# Revit family: 879-005X99-001-DN65-600
name_source: partatom
category: Pipe Accessories
units: mm (PartAtom-declared; Revit-internal decimal feet)

## family parameters
Always vertical = Yes
Cut with Voids When Loaded = No
Part Type = Valve - Breaks Into
Round Connector Dimension = Use Diameter
Shared = No
Work Plane-Based = No

## types (42) — shared parameters
879-0065-00-14400559999 = DN65_PN10/16
879-0065-00-144005599A0 = DN65_PN10/16
879-0080-00-14400559999 = DN80_PN10/16
879-0080-00-144005599A0 = DN80_PN10/16
879-0100-00-14400559999 = DN100_PN10/16
879-0100-00-144005599A0 = DN100_PN10/16
879-0125-00-14400559999 = DN125_PN10/16
879-0125-00-144005599A0 = DN125_PN10/16
879-0150-00-14400559999 = DN150_PN10/16
879-0150-00-144005599A0 = DN150_PN10/16
879-0200-00-04400559999 = DN200_PN10
879-0200-00-044005599A0 = DN200_PN10
879-0200-00-14400559999 = DN200_PN16
879-0200-00-144005599A0 = DN200_PN16
879-0250-00-04400559999 = DN250_PN10
879-0250-00-044005599A0 = DN250_PN10
879-0250-00-14400559999 = DN250_PN16
879-0250-00-144005599A0 = DN250_PN16
879-0300-00-04400559999 = DN300_PN10
879-0300-00-044005599A0 = DN300_PN10
879-0300-00-14400559999 = DN300_PN16
879-0300-00-144005599A0 = DN300_PN16
879-0350-00-04400559999 = DN350_PN10
879-0350-00-044005599A0 = DN350_PN10
879-0350-00-14400559999 = DN350_PN16
879-0350-00-144005599A0 = DN350_PN16
879-0400-00-04400559999 = DN400_PN10
879-0400-00-044005599A0 = DN400_PN10
879-0400-00-14400559999 = DN400_PN16
879-0400-00-144005599A0 = DN400_PN16
879-0450-00-04400559999 = DN450_PN10
879-0450-00-044005599A0 = DN450_PN10
879-0450-00-14400559999 = DN450_PN16
879-0450-00-144005599A0 = DN450_PN16
879-0500-00-04400559999 = DN500_PN10
879-0500-00-044005599A0 = DN500_PN10
879-0500-00-14400559999 = DN500_PN16
879-0500-00-144005599A0 = DN500_PN16
879-0600-00-04400559999 = DN600_PN10
879-0600-00-044005599A0 = DN600_PN10
879-0600-00-14400559999 = DN600_PN16
879-0600-00-144005599A0 = DN600_PN16
Body_wall_thickness = 10 mm  [stored 0.0328084 ft]
Description_ = AVK MODULATING FLOAT LEVEL CONTROL VALVE
Search_Table = 879-005X99-001-DN65-600
URL product pages = https://www.avkvalves.com

## per-type parameters (varying)
- 879-0065-00-14400559999_DN65_PN10/16: Body_Collar_Dia=22 mm  [stored 0.0721785 ft]; Body_Collar_Dia_2=15 mm  [stored 0.0492126 ft]; Body_Flange_Dia=83 mm; Body_Flange_Dia_2=88 mm; Body_Height_1=83 mm; Body_Height_2=36 mm  [stored 0.11811 ft]; Body_Height_3=58 mm; Body_Height_4=51 mm; Body_Top_Dia=10 mm  [stored 0.0328084 ft]; Body_Top_Dia_2=8 mm  [stored 0.0262467 ft]; Body_With_Dia=58 mm; Body_With_Dia_1=73 mm; Body_With_Dia_2=73 mm; Bolt_support=223 mm; Bolt_support_2=112 mm; Bolt_support_Dia=12 mm  [stored 0.0393701 ft]; Bolt_support_lenght=53 mm; Bolt_support_lenght_2=63 mm; Bottom_profile=16 mm  [stored 0.0524934 ft]; D1=59 mm; D3=93 mm; DN=65 mm; Fillet_Length=6 mm  [stored 0.019685 ft]; Fillet_Length_2=24 mm  [stored 0.0787402 ft]; Flange_thickness=19 mm  [stored 0.062336 ft]; H3=339 mm; H3_Ref=322 mm; H3_Ref_2=154 mm; ID=33 mm; L=290 mm; PG_Dia=33 mm; PG_Ref=55 mm; PG_depth=8 mm  [stored 0.0262467 ft]; PG_height=211 mm; PG_height_1=194 mm; PG_ref=43 mm  [stored 0.141076 ft]; PR_1=20 mm  [stored 0.0656168 ft]; P_lenght=39 mm  [stored 0.127953 ft]; Pilot_Dia_1=18 mm; Pilot_Dia_2=35 mm  [stored 0.114829 ft]; Pilot_Dia_3=12 mm  [stored 0.0393701 ft]; Pilot_Dia_4=6 mm  [stored 0.019685 ft]; Pilot_Dia_5=4 mm  [stored 0.0131234 ft]; Pilot_top_1=219 mm; Pilot_top_ref=17 mm; Profile1_Height=117 mm; Profile1_Length=25 mm  [stored 0.082021 ft]; Profile1_Length_2=17 mm; Profile_Dia=6 mm  [stored 0.019685 ft]; Profile_Dia_2=6 mm  [stored 0.019685 ft]; Profile_Dia_3=12 mm  [stored 0.0393701 ft]; Profile_height ref=41 mm  [stored 0.134514 ft]; T_Height=89 mm; T_Height_2=76 mm; T_Height_Ref_1=13 mm  [stored 0.0426509 ft]; T_Height_Ref_2=15 mm  [stored 0.0492126 ft]; Top_Profile=134 mm; Top_Profile_Ref=139 mm; W=244 mm; W_Ref=238 mm
- 879-0065-00-144005599A0_DN65_PN10/16: Body_Collar_Dia=22 mm  [stored 0.0721785 ft]; Body_Collar_Dia_2=15 mm  [stored 0.0492126 ft]; Body_Flange_Dia=83 mm; Body_Flange_Dia_2=88 mm; Body_Height_1=83 mm; Body_Height_2=36 mm  [stored 0.11811 ft]; Body_Height_3=100 mm; Body_Height_4=51 mm; Body_Top_Dia=10 mm  [stored 0.0328084 ft]; Body_Top_Dia_2=8 mm  [stored 0.0262467 ft]; Body_With_Dia=58 mm; Body_With_Dia_1=73 mm; Body_With_Dia_2=73 mm; Bolt_support=223 mm; Bolt_support_2=112 mm; Bolt_support_Dia=12 mm  [stored 0.0393701 ft]; Bolt_support_lenght=53 mm; Bolt_support_lenght_2=63 mm; Bottom_profile=16 mm  [stored 0.0524934 ft]; D1=59 mm; D3=93 mm; DN=65 mm; Fillet_Length=6 mm  [stored 0.019685 ft]; Fillet_Length_2=24 mm  [stored 0.0787402 ft]; Flange_thickness=19 mm  [stored 0.062336 ft]; H3=424 mm; H3_Ref=385 mm; H3_Ref_2=154 mm; ID=33 mm; L=290 mm; PG_Dia=33 mm; PG_Ref=55 mm; PG_depth=8 mm  [stored 0.0262467 ft]; PG_height=244 mm; PG_height_1=227 mm; PG_ref=43 mm  [stored 0.141076 ft]; PR_1=35 mm  [stored 0.114829 ft]; P_lenght=39 mm  [stored 0.127953 ft]; Pilot_Dia_1=18 mm; Pilot_Dia_2=35 mm  [stored 0.114829 ft]; Pilot_Dia_3=12 mm  [stored 0.0393701 ft]; Pilot_Dia_4=6 mm  [stored 0.019685 ft]; Pilot_Dia_5=4 mm  [stored 0.0131234 ft]; Pilot_top_1=283 mm; Pilot_top_ref=39 mm  [stored 0.127953 ft]; Profile1_Height=135 mm; Profile1_Length=25 mm  [stored 0.082021 ft]; Profile1_Length_2=17 mm; Profile_Dia=6 mm  [stored 0.019685 ft]; Profile_Dia_2=6 mm  [stored 0.019685 ft]; Profile_Dia_3=12 mm  [stored 0.0393701 ft]; Profile_height ref=41 mm  [stored 0.134514 ft]; T_Height=156 mm; T_Height_2=133 mm; T_Height_Ref_1=22 mm  [stored 0.0721785 ft]; T_Height_Ref_2=26 mm; Top_Profile=134 mm; Top_Profile_Ref=139 mm; W=244 mm; W_Ref=238 mm
- 879-0080-00-14400559999_DN80_PN10/16: Body_Collar_Dia=24 mm  [stored 0.0787402 ft]; Body_Collar_Dia_2=16 mm  [stored 0.0524934 ft]; Body_Flange_Dia=89 mm; Body_Flange_Dia_2=94 mm; Body_Height_1=89 mm; Body_Height_2=39 mm  [stored 0.127953 ft]; Body_Height_3=62 mm; Body_Height_4=54 mm; Body_Top_Dia=10 mm  [stored 0.0328084 ft]; Body_Top_Dia_2=9 mm  [stored 0.0295276 ft]; Body_With_Dia=62 mm; Body_With_Dia_1=78 mm; Body_With_Dia_2=78 mm; Bolt_support=238 mm; Bolt_support_2=119 mm; Bolt_support_Dia=12 mm  [stored 0.0393701 ft]; Bolt_support_lenght=60 mm; Bolt_support_lenght_2=70 mm; Bottom_profile=20 mm  [stored 0.0656168 ft]; D1=66 mm; D3=100 mm; DN=80 mm; Fillet_Length=6 mm  [stored 0.019685 ft]; Fillet_Length_2=24 mm  [stored 0.0787402 ft]; Flange_thickness=19 mm  [stored 0.062336 ft]; H3=362 mm; H3_Ref=343 mm; H3_Ref_2=162 mm; ID=40 mm  [stored 0.131234 ft]; L=310 mm; PG_Dia=40 mm  [stored 0.131234 ft]; PG_Ref=59 mm; PG_depth=8 mm  [stored 0.0262467 ft]; PG_height=242 mm; PG_height_1=222 mm; PG_ref=50 mm; PR_1=17 mm; P_lenght=43 mm  [stored 0.141076 ft]; Pilot_Dia_1=20 mm  [stored 0.0656168 ft]; Pilot_Dia_2=39 mm  [stored 0.127953 ft]; Pilot_Dia_3=13 mm  [stored 0.0426509 ft]; Pilot_Dia_4=7 mm  [stored 0.0229659 ft]; Pilot_Dia_5=4 mm  [stored 0.0131234 ft]; Pilot_top_1=233 mm; Pilot_top_ref=19 mm  [stored 0.062336 ft]; Profile1_Height=144 mm; Profile1_Length=27 mm; Profile1_Length_2=18 mm; Profile_Dia=6 mm  [stored 0.019685 ft]; Profile_Dia_2=6 mm  [stored 0.019685 ft]; Profile_Dia_3=12 mm  [stored 0.0393701 ft]; Profile_height ref=41 mm  [stored 0.134514 ft]; T_Height=77 mm; T_Height_2=66 mm; T_Height_Ref_1=11 mm  [stored 0.0360892 ft]; T_Height_Ref_2=13 mm  [stored 0.0426509 ft]; Top_Profile=143 mm; Top_Profile_Ref=148 mm; W=257 mm; W_Ref=251 mm
- 879-0080-00-144005599A0_DN80_PN10/16: Body_Collar_Dia=24 mm  [stored 0.0787402 ft]; Body_Collar_Dia_2=16 mm  [stored 0.0524934 ft]; Body_Flange_Dia=89 mm; Body_Flange_Dia_2=94 mm; Body_Height_1=89 mm; Body_Height_2=39 mm  [stored 0.127953 ft]; Body_Height_3=110 mm; Body_Height_4=54 mm; Body_Top_Dia=10 mm  [stored 0.0328084 ft]; Body_Top_Dia_2=9 mm  [stored 0.0295276 ft]; Body_With_Dia=62 mm; Body_With_Dia_1=78 mm; Body_With_Dia_2=78 mm; Bolt_support=238 mm; Bolt_support_2=119 mm; Bolt_support_Dia=12 mm  [stored 0.0393701 ft]; Bolt_support_lenght=60 mm; Bolt_support_lenght_2=70 mm; Bottom_profile=20 mm  [stored 0.0656168 ft]; D1=66 mm; D3=100 mm; DN=80 mm; Fillet_Length=6 mm  [stored 0.019685 ft]; Fillet_Length_2=24 mm  [stored 0.0787402 ft]; Flange_thickness=19 mm  [stored 0.062336 ft]; H3=447 mm; H3_Ref=410 mm; H3_Ref_2=162 mm; ID=40 mm  [stored 0.131234 ft]; L=310 mm; PG_Dia=40 mm  [stored 0.131234 ft]; PG_Ref=59 mm; PG_depth=8 mm  [stored 0.0262467 ft]; PG_height=253 mm; PG_height_1=233 mm; PG_ref=50 mm; PR_1=39 mm  [stored 0.127953 ft]; P_lenght=43 mm  [stored 0.141076 ft]; Pilot_Dia_1=20 mm  [stored 0.0656168 ft]; Pilot_Dia_2=39 mm  [stored 0.127953 ft]; Pilot_Dia_3=13 mm  [stored 0.0426509 ft]; Pilot_Dia_4=7 mm  [stored 0.0229659 ft]; Pilot_Dia_5=4 mm  [stored 0.0131234 ft]; Pilot_top_1=300 mm; Pilot_top_ref=37 mm; Profile1_Height=133 mm; Profile1_Length=27 mm; Profile1_Length_2=18 mm; Profile_Dia=6 mm  [stored 0.019685 ft]; Profile_Dia_2=6 mm  [stored 0.019685 ft]; Profile_Dia_3=12 mm  [stored 0.0393701 ft]; Profile_height ref=41 mm  [stored 0.134514 ft]; T_Height=173 mm; T_Height_2=148 mm; T_Height_Ref_1=25 mm  [stored 0.082021 ft]; T_Height_Ref_2=29 mm; Top_Profile=143 mm; Top_Profile_Ref=148 mm; W=257 mm; W_Ref=251 mm
- 879-0100-00-14400559999_DN100_PN10/16: Body_Collar_Dia=27 mm; Body_Collar_Dia_2=18 mm; Body_Flange_Dia=100 mm; Body_Flange_Dia_2=106 mm; Body_Height_1=100 mm; Body_Height_2=44 mm; Body_Height_3=50 mm; Body_Height_4=59 mm; Body_Top_Dia=12 mm  [stored 0.0393701 ft]; Body_Top_Dia_2=10 mm  [stored 0.0328084 ft]; Body_With_Dia=70 mm; Body_With_Dia_1=88 mm; Body_With_Dia_2=88 mm; Bolt_support=269 mm; Bolt_support_2=135 mm; Bolt_support_Dia=12 mm  [stored 0.0393701 ft]; Bolt_support_lenght=70 mm; Bolt_support_lenght_2=80 mm; Bottom_profile=25 mm  [stored 0.082021 ft]; D1=78 mm; D3=110 mm; DN=100 mm; Fillet_Length=6 mm  [stored 0.019685 ft]; Fillet_Length_2=24 mm  [stored 0.0787402 ft]; Flange_thickness=19 mm  [stored 0.062336 ft]; H3=376 mm; H3_Ref=357 mm; H3_Ref_2=179 mm; ID=50 mm; L=350 mm; PG_Dia=50 mm; PG_Ref=67 mm; PG_depth=8 mm  [stored 0.0262467 ft]; PG_height=258 mm; PG_height_1=233 mm; PG_ref=60 mm; PR_1=17 mm; P_lenght=48 mm; Pilot_Dia_1=22 mm  [stored 0.0721785 ft]; Pilot_Dia_2=44 mm; Pilot_Dia_3=15 mm  [stored 0.0492126 ft]; Pilot_Dia_4=7 mm  [stored 0.0229659 ft]; Pilot_Dia_5=5 mm  [stored 0.0164042 ft]; Pilot_top_1=237 mm; Pilot_top_ref=19 mm  [stored 0.062336 ft]; Profile1_Height=150 mm; Profile1_Length=30 mm  [stored 0.0984252 ft]; Profile1_Length_2=20 mm  [stored 0.0656168 ft]; Profile_Dia=6 mm  [stored 0.019685 ft]; Profile_Dia_2=6 mm  [stored 0.019685 ft]; Profile_Dia_3=12 mm  [stored 0.0393701 ft]; Profile_height ref=41 mm  [stored 0.134514 ft]; T_Height=75 mm; T_Height_2=64 mm; T_Height_Ref_1=11 mm  [stored 0.0360892 ft]; T_Height_Ref_2=13 mm  [stored 0.0426509 ft]; Top_Profile=162 mm; Top_Profile_Ref=167 mm; W=276 mm; W_Ref=270 mm
- 879-0100-00-144005599A0_DN100_PN10/16: Body_Collar_Dia=27 mm; Body_Collar_Dia_2=18 mm; Body_Flange_Dia=100 mm; Body_Flange_Dia_2=106 mm; Body_Height_1=100 mm; Body_Height_2=44 mm; Body_Height_3=100 mm; Body_Height_4=59 mm; Body_Top_Dia=12 mm  [stored 0.0393701 ft]; Body_Top_Dia_2=10 mm  [stored 0.0328084 ft]; Body_With_Dia=70 mm; Body_With_Dia_1=88 mm; Body_With_Dia_2=88 mm; Bolt_support=269 mm; Bolt_support_2=135 mm; Bolt_support_Dia=12 mm  [stored 0.0393701 ft]; Bolt_support_lenght=70 mm; Bolt_support_lenght_2=80 mm; Bottom_profile=25 mm  [stored 0.082021 ft]; D1=78 mm; D3=110 mm; DN=100 mm; Fillet_Length=6 mm  [stored 0.019685 ft]; Fillet_Length_2=24 mm  [stored 0.0787402 ft]; Flange_thickness=19 mm  [stored 0.062336 ft]; H3=461 mm; H3_Ref=425 mm; H3_Ref_2=179 mm; ID=50 mm; L=350 mm; PG_Dia=50 mm; PG_Ref=67 mm; PG_depth=8 mm  [stored 0.0262467 ft]; PG_height=270 mm; PG_height_1=245 mm; PG_ref=60 mm; PR_1=38 mm; P_lenght=48 mm; Pilot_Dia_1=22 mm  [stored 0.0721785 ft]; Pilot_Dia_2=44 mm; Pilot_Dia_3=15 mm  [stored 0.0492126 ft]; Pilot_Dia_4=7 mm  [stored 0.0229659 ft]; Pilot_Dia_5=5 mm  [stored 0.0164042 ft]; Pilot_top_1=305 mm; Pilot_top_ref=36 mm  [stored 0.11811 ft]; Profile1_Height=141 mm; Profile1_Length=30 mm  [stored 0.0984252 ft]; Profile1_Length_2=20 mm  [stored 0.0656168 ft]; Profile_Dia=6 mm  [stored 0.019685 ft]; Profile_Dia_2=6 mm  [stored 0.019685 ft]; Profile_Dia_3=12 mm  [stored 0.0393701 ft]; Profile_height ref=41 mm  [stored 0.134514 ft]; T_Height=169 mm; T_Height_2=145 mm; T_Height_Ref_1=24 mm  [stored 0.0787402 ft]; T_Height_Ref_2=28 mm  [stored 0.0918635 ft]; Top_Profile=162 mm; Top_Profile_Ref=167 mm; W=276 mm; W_Ref=270 mm
- 879-0125-00-14400559999_DN125_PN10/16: Body_Collar_Dia=31 mm  [stored 0.101706 ft]; Body_Collar_Dia_2=20 mm  [stored 0.0656168 ft]; Body_Flange_Dia=114 mm; Body_Flange_Dia_2=121 mm; Body_Height_1=114 mm; Body_Height_2=50 mm; Body_Height_3=35 mm  [stored 0.114829 ft]; Body_Height_4=65 mm; Body_Top_Dia=13 mm  [stored 0.0426509 ft]; Body_Top_Dia_2=11 mm  [stored 0.0360892 ft]; Body_With_Dia=80 mm; Body_With_Dia_1=100 mm; Body_With_Dia_2=100 mm; Bolt_support=308 mm; Bolt_support_2=154 mm; Bolt_support_Dia=12 mm  [stored 0.0393701 ft]; Bolt_support_lenght=83 mm; Bolt_support_lenght_2=93 mm; Bottom_profile=31 mm  [stored 0.101706 ft]; D1=92 mm; D3=125 mm; DN=125 mm; Fillet_Length=6 mm  [stored 0.019685 ft]; Fillet_Length_2=24 mm  [stored 0.0787402 ft]; Flange_thickness=19 mm  [stored 0.062336 ft]; H3=395 mm; H3_Ref=377 mm; H3_Ref_2=199 mm; ID=63 mm; L=400 mm; PG_Dia=63 mm; PG_Ref=76 mm; PG_depth=8 mm  [stored 0.0262467 ft]; PG_height=283 mm; PG_height_1=252 mm; PG_ref=73 mm; PR_1=14 mm  [stored 0.0459318 ft]; P_lenght=56 mm; Pilot_Dia_1=26 mm; Pilot_Dia_2=51 mm; Pilot_Dia_3=17 mm; Pilot_Dia_4=9 mm  [stored 0.0295276 ft]; Pilot_Dia_5=6 mm  [stored 0.019685 ft]; Pilot_top_1=242 mm; Pilot_top_ref=18 mm; Profile1_Height=165 mm; Profile1_Length=34 mm; Profile1_Length_2=23 mm  [stored 0.0754593 ft]; Profile_Dia=6 mm  [stored 0.019685 ft]; Profile_Dia_2=6 mm  [stored 0.019685 ft]; Profile_Dia_3=12 mm  [stored 0.0393701 ft]; Profile_height ref=41 mm  [stored 0.134514 ft]; T_Height=64 mm; T_Height_2=55 mm; T_Height_Ref_1=9 mm  [stored 0.0295276 ft]; T_Height_Ref_2=11 mm  [stored 0.0360892 ft]; Top_Profile=185 mm; Top_Profile_Ref=190 mm; W=296 mm; W_Ref=290 mm
- 879-0125-00-144005599A0_DN125_PN10/16: Body_Collar_Dia=31 mm  [stored 0.101706 ft]; Body_Collar_Dia_2=20 mm  [stored 0.0656168 ft]; Body_Flange_Dia=114 mm; Body_Flange_Dia_2=121 mm; Body_Height_1=114 mm; Body_Height_2=50 mm; Body_Height_3=90 mm; Body_Height_4=65 mm; Body_Top_Dia=13 mm  [stored 0.0426509 ft]; Body_Top_Dia_2=11 mm  [stored 0.0360892 ft]; Body_With_Dia=80 mm; Body_With_Dia_1=100 mm; Body_With_Dia_2=100 mm; Bolt_support=308 mm; Bolt_support_2=154 mm; Bolt_support_Dia=12 mm  [stored 0.0393701 ft]; Bolt_support_lenght=83 mm; Bolt_support_lenght_2=93 mm; Bottom_profile=31 mm  [stored 0.101706 ft]; D1=92 mm; D3=125 mm; DN=125 mm; Fillet_Length=6 mm  [stored 0.019685 ft]; Fillet_Length_2=24 mm  [stored 0.0787402 ft]; Flange_thickness=19 mm  [stored 0.062336 ft]; H3=480 mm; H3_Ref=447 mm; H3_Ref_2=199 mm; ID=63 mm; L=400 mm; PG_Dia=63 mm; PG_Ref=76 mm; PG_depth=8 mm  [stored 0.0262467 ft]; PG_height=302 mm; PG_height_1=271 mm; PG_ref=73 mm; PR_1=34 mm; P_lenght=56 mm; Pilot_Dia_1=26 mm; Pilot_Dia_2=51 mm; Pilot_Dia_3=17 mm; Pilot_Dia_4=9 mm  [stored 0.0295276 ft]; Pilot_Dia_5=6 mm  [stored 0.019685 ft]; Pilot_top_1=312 mm; Pilot_top_ref=33 mm; Profile1_Height=165 mm; Profile1_Length=34 mm; Profile1_Length_2=23 mm  [stored 0.0754593 ft]; Profile_Dia=6 mm  [stored 0.019685 ft]; Profile_Dia_2=6 mm  [stored 0.019685 ft]; Profile_Dia_3=12 mm  [stored 0.0393701 ft]; Profile_height ref=41 mm  [stored 0.134514 ft]; T_Height=149 mm; T_Height_2=128 mm; T_Height_Ref_1=21 mm  [stored 0.0688976 ft]; T_Height_Ref_2=25 mm  [stored 0.082021 ft]; Top_Profile=185 mm; Top_Profile_Ref=190 mm; W=296 mm; W_Ref=290 mm
- 879-0150-00-14400559999_DN150_PN10/16: Body_Collar_Dia=37 mm; Body_Collar_Dia_2=24 mm  [stored 0.0787402 ft]; Body_Flange_Dia=137 mm; Body_Flange_Dia_2=145 mm; Body_Height_1=137 mm; Body_Height_2=60 mm; Body_Height_3=30 mm  [stored 0.0984252 ft]; Body_Height_4=75 mm; Body_Top_Dia=16 mm  [stored 0.0524934 ft]; Body_Top_Dia_2=13 mm  [stored 0.0426509 ft]; Body_With_Dia=96 mm; Body_With_Dia_1=120 mm; Body_With_Dia_2=120 mm; Bolt_support=369 mm; Bolt_support_2=185 mm; Bolt_support_Dia=16 mm  [stored 0.0524934 ft]; Bolt_support_lenght=95 mm; Bolt_support_lenght_2=105 mm; Bottom_profile=38 mm; D1=106 mm; D3=143 mm; DN=150 mm; Fillet_Length=8 mm  [stored 0.0262467 ft]; Fillet_Length_2=32 mm  [stored 0.104987 ft]; Flange_thickness=19 mm  [stored 0.062336 ft]; H3=429 mm; H3_Ref=417 mm; H3_Ref_2=232 mm; ID=75 mm; L=480 mm; PG_Dia=50 mm; PG_Ref=91 mm; PG_depth=11 mm  [stored 0.0360892 ft]; PG_height=299 mm; PG_height_1=274 mm; PG_ref=85 mm; PR_1=11 mm  [stored 0.0360892 ft]; P_lenght=68 mm; Pilot_Dia_1=31 mm  [stored 0.101706 ft]; Pilot_Dia_2=62 mm; Pilot_Dia_3=21 mm  [stored 0.0688976 ft]; Pilot_Dia_4=10 mm  [stored 0.0328084 ft]; Pilot_Dia_5=7 mm  [stored 0.0229659 ft]; Pilot_top_1=264 mm; Pilot_top_ref=12 mm  [stored 0.0393701 ft]; Profile1_Height=195 mm; Profile1_Length=39 mm  [stored 0.127953 ft]; Profile1_Length_2=26 mm; Profile_Dia=8 mm  [stored 0.0262467 ft]; Profile_Dia_2=8 mm  [stored 0.0262467 ft]; Profile_Dia_3=16 mm  [stored 0.0524934 ft]; Profile_height ref=43 mm  [stored 0.141076 ft]; T_Height=49 mm; T_Height_2=42 mm  [stored 0.137795 ft]; T_Height_Ref_1=7 mm  [stored 0.0229659 ft]; T_Height_Ref_2=8 mm  [stored 0.0262467 ft]; Top_Profile=222 mm; Top_Profile_Ref=227 mm; W=302 mm; W_Ref=294 mm
- 879-0150-00-144005599A0_DN150_PN10/16: Body_Collar_Dia=37 mm; Body_Collar_Dia_2=24 mm  [stored 0.0787402 ft]; Body_Flange_Dia=137 mm; Body_Flange_Dia_2=145 mm; Body_Height_1=137 mm; Body_Height_2=60 mm; Body_Height_3=115 mm; Body_Height_4=75 mm; Body_Top_Dia=16 mm  [stored 0.0524934 ft]; Body_Top_Dia_2=13 mm  [stored 0.0426509 ft]; Body_With_Dia=96 mm; Body_With_Dia_1=120 mm; Body_With_Dia_2=120 mm; Bolt_support=369 mm; Bolt_support_2=185 mm; Bolt_support_Dia=16 mm  [stored 0.0524934 ft]; Bolt_support_lenght=95 mm; Bolt_support_lenght_2=105 mm; Bottom_profile=38 mm; D1=106 mm; D3=143 mm; DN=150 mm; Fillet_Length=8 mm  [stored 0.0262467 ft]; Fillet_Length_2=32 mm  [stored 0.104987 ft]; Flange_thickness=19 mm  [stored 0.062336 ft]; H3=514 mm; H3_Ref=502 mm; H3_Ref_2=232 mm; ID=75 mm; L=480 mm; PG_Dia=50 mm; PG_Ref=91 mm; PG_depth=11 mm  [stored 0.0360892 ft]; PG_height=318 mm; PG_height_1=293 mm; PG_ref=85 mm; PR_1=30 mm  [stored 0.0984252 ft]; P_lenght=68 mm; Pilot_Dia_1=31 mm  [stored 0.101706 ft]; Pilot_Dia_2=62 mm; Pilot_Dia_3=21 mm  [stored 0.0688976 ft]; Pilot_Dia_4=10 mm  [stored 0.0328084 ft]; Pilot_Dia_5=7 mm  [stored 0.0229659 ft]; Pilot_top_1=349 mm; Pilot_top_ref=12 mm  [stored 0.0393701 ft]; Profile1_Height=195 mm; Profile1_Length=39 mm  [stored 0.127953 ft]; Profile1_Length_2=26 mm; Profile_Dia=8 mm  [stored 0.0262467 ft]; Profile_Dia_2=8 mm  [stored 0.0262467 ft]; Profile_Dia_3=16 mm  [stored 0.0524934 ft]; Profile_height ref=43 mm  [stored 0.141076 ft]; T_Height=134 mm; T_Height_2=114 mm; T_Height_Ref_1=19 mm  [stored 0.062336 ft]; T_Height_Ref_2=22 mm  [stored 0.0721785 ft]; Top_Profile=222 mm; Top_Profile_Ref=227 mm; W=302 mm; W_Ref=294 mm
- 879-0200-00-04400559999_DN200_PN10: Body_Collar_Dia=46 mm; Body_Collar_Dia_2=30 mm  [stored 0.0984252 ft]; Body_Flange_Dia=171 mm; Body_Flange_Dia_2=182 mm; Body_Height_1=171 mm; Body_Height_2=75 mm; Body_Height_3=100 mm; Body_Height_4=90 mm; Body_Top_Dia=20 mm  [stored 0.0656168 ft]; Body_Top_Dia_2=17 mm; Body_With_Dia=120 mm; Body_With_Dia_1=150 mm; Body_With_Dia_2=150 mm; Bolt_support=462 mm; Bolt_support_2=231 mm; Bolt_support_Dia=20 mm  [stored 0.0656168 ft]; Bolt_support_lenght=120 mm; Bolt_support_lenght_2=130 mm; Bottom_profile=50 mm; D1=133 mm; D3=170 mm; DN=200 mm; Fillet_Length=10 mm  [stored 0.0328084 ft]; Fillet_Length_2=40 mm  [stored 0.131234 ft]; Flange_thickness=20 mm  [stored 0.0656168 ft]; H3=588 mm; H3_Ref=570 mm; H3_Ref_2=281 mm; ID=100 mm; L=600 mm; PG_Dia=67 mm; PG_Ref=114 mm; PG_depth=14 mm  [stored 0.0459318 ft]; PG_height=380 mm; PG_height_1=347 mm; PG_ref=110 mm; PR_1=31 mm  [stored 0.101706 ft]; P_lenght=85 mm; Pilot_Dia_1=39 mm  [stored 0.127953 ft]; Pilot_Dia_2=77 mm; Pilot_Dia_3=26 mm; Pilot_Dia_4=13 mm  [stored 0.0426509 ft]; Pilot_Dia_5=9 mm  [stored 0.0295276 ft]; Pilot_top_1=390 mm; Pilot_top_ref=18 mm; Profile1_Height=238 mm; Profile1_Length=46 mm; Profile1_Length_2=31 mm  [stored 0.101706 ft]; Profile_Dia=10 mm  [stored 0.0328084 ft]; Profile_Dia_2=10 mm  [stored 0.0328084 ft]; Profile_Dia_3=20 mm  [stored 0.0656168 ft]; Profile_height ref=45 mm; T_Height=135 mm; T_Height_2=116 mm; T_Height_Ref_1=19 mm  [stored 0.062336 ft]; T_Height_Ref_2=23 mm  [stored 0.0754593 ft]; Top_Profile=277 mm; Top_Profile_Ref=282 mm; W=410 mm; W_Ref=400 mm
- 879-0200-00-044005599A0_DN200_PN10: Body_Collar_Dia=46 mm; Body_Collar_Dia_2=30 mm  [stored 0.0984252 ft]; Body_Flange_Dia=171 mm; Body_Flange_Dia_2=182 mm; Body_Height_1=171 mm; Body_Height_2=75 mm; Body_Height_3=170 mm; Body_Height_4=90 mm; Body_Top_Dia=20 mm  [stored 0.0656168 ft]; Body_Top_Dia_2=17 mm; Body_With_Dia=120 mm; Body_With_Dia_1=150 mm; Body_With_Dia_2=150 mm; Bolt_support=462 mm; Bolt_support_2=231 mm; Bolt_support_Dia=20 mm  [stored 0.0656168 ft]; Bolt_support_lenght=120 mm; Bolt_support_lenght_2=130 mm; Bottom_profile=50 mm; D1=133 mm; D3=170 mm; DN=200 mm; Fillet_Length=10 mm  [stored 0.0328084 ft]; Fillet_Length_2=40 mm  [stored 0.131234 ft]; Flange_thickness=20 mm  [stored 0.0656168 ft]; H3=688 mm; H3_Ref=655 mm; H3_Ref_2=281 mm; ID=100 mm; L=600 mm; PG_Dia=67 mm; PG_Ref=114 mm; PG_depth=14 mm  [stored 0.0459318 ft]; PG_height=404 mm; PG_height_1=371 mm; PG_ref=110 mm; PR_1=53 mm; P_lenght=85 mm; Pilot_Dia_1=39 mm  [stored 0.127953 ft]; Pilot_Dia_2=77 mm; Pilot_Dia_3=26 mm; Pilot_Dia_4=13 mm  [stored 0.0426509 ft]; Pilot_Dia_5=9 mm  [stored 0.0295276 ft]; Pilot_top_1=475 mm; Pilot_top_ref=33 mm; Profile1_Height=240 mm; Profile1_Length=46 mm; Profile1_Length_2=31 mm  [stored 0.101706 ft]; Profile_Dia=10 mm  [stored 0.0328084 ft]; Profile_Dia_2=10 mm  [stored 0.0328084 ft]; Profile_Dia_3=20 mm  [stored 0.0656168 ft]; Profile_height ref=45 mm; T_Height=233 mm; T_Height_2=200 mm; T_Height_Ref_1=33 mm; T_Height_Ref_2=39 mm  [stored 0.127953 ft]; Top_Profile=277 mm; Top_Profile_Ref=282 mm; W=410 mm; W_Ref=400 mm
- 879-0200-00-14400559999_DN200_PN16: Body_Collar_Dia=46 mm; Body_Collar_Dia_2=30 mm  [stored 0.0984252 ft]; Body_Flange_Dia=171 mm; Body_Flange_Dia_2=182 mm; Body_Height_1=171 mm; Body_Height_2=75 mm; Body_Height_3=100 mm; Body_Height_4=90 mm; Body_Top_Dia=20 mm  [stored 0.0656168 ft]; Body_Top_Dia_2=17 mm; Body_With_Dia=120 mm; Body_With_Dia_1=150 mm; Body_With_Dia_2=150 mm; Bolt_support=462 mm; Bolt_support_2=231 mm; Bolt_support_Dia=20 mm  [stored 0.0656168 ft]; Bolt_support_lenght=120 mm; Bolt_support_lenght_2=130 mm; Bottom_profile=50 mm; D1=133 mm; D3=170 mm; DN=200 mm; Fillet_Length=10 mm  [stored 0.0328084 ft]; Fillet_Length_2=40 mm  [stored 0.131234 ft]; Flange_thickness=20 mm  [stored 0.0656168 ft]; H3=588 mm; H3_Ref=570 mm; H3_Ref_2=281 mm; ID=100 mm; L=600 mm; PG_Dia=67 mm; PG_Ref=114 mm; PG_depth=14 mm  [stored 0.0459318 ft]; PG_height=380 mm; PG_height_1=347 mm; PG_ref=110 mm; PR_1=31 mm  [stored 0.101706 ft]; P_lenght=85 mm; Pilot_Dia_1=39 mm  [stored 0.127953 ft]; Pilot_Dia_2=77 mm; Pilot_Dia_3=26 mm; Pilot_Dia_4=13 mm  [stored 0.0426509 ft]; Pilot_Dia_5=9 mm  [stored 0.0295276 ft]; Pilot_top_1=390 mm; Pilot_top_ref=18 mm; Profile1_Height=238 mm; Profile1_Length=46 mm; Profile1_Length_2=31 mm  [stored 0.101706 ft]; Profile_Dia=10 mm  [stored 0.0328084 ft]; Profile_Dia_2=10 mm  [stored 0.0328084 ft]; Profile_Dia_3=20 mm  [stored 0.0656168 ft]; Profile_height ref=45 mm; T_Height=135 mm; T_Height_2=116 mm; T_Height_Ref_1=19 mm  [stored 0.062336 ft]; T_Height_Ref_2=23 mm  [stored 0.0754593 ft]; Top_Profile=277 mm; Top_Profile_Ref=282 mm; W=410 mm; W_Ref=400 mm
- 879-0200-00-144005599A0_DN200_PN16: Body_Collar_Dia=46 mm; Body_Collar_Dia_2=30 mm  [stored 0.0984252 ft]; Body_Flange_Dia=171 mm; Body_Flange_Dia_2=182 mm; Body_Height_1=171 mm; Body_Height_2=75 mm; Body_Height_3=165 mm; Body_Height_4=90 mm; Body_Top_Dia=20 mm  [stored 0.0656168 ft]; Body_Top_Dia_2=17 mm; Body_With_Dia=120 mm; Body_With_Dia_1=150 mm; Body_With_Dia_2=150 mm; Bolt_support=462 mm; Bolt_support_2=231 mm; Bolt_support_Dia=20 mm  [stored 0.0656168 ft]; Bolt_support_lenght=120 mm; Bolt_support_lenght_2=130 mm; Bottom_profile=50 mm; D1=133 mm; D3=170 mm; DN=200 mm; Fillet_Length=10 mm  [stored 0.0328084 ft]; Fillet_Length_2=40 mm  [stored 0.131234 ft]; Flange_thickness=20 mm  [stored 0.0656168 ft]; H3=688 mm; H3_Ref=652 mm; H3_Ref_2=281 mm; ID=100 mm; L=600 mm; PG_Dia=67 mm; PG_Ref=114 mm; PG_depth=14 mm  [stored 0.0459318 ft]; PG_height=404 mm; PG_height_1=371 mm; PG_ref=110 mm; PR_1=53 mm; P_lenght=85 mm; Pilot_Dia_1=39 mm  [stored 0.127953 ft]; Pilot_Dia_2=77 mm; Pilot_Dia_3=26 mm; Pilot_Dia_4=13 mm  [stored 0.0426509 ft]; Pilot_Dia_5=9 mm  [stored 0.0295276 ft]; Pilot_top_1=472 mm; Pilot_top_ref=36 mm  [stored 0.11811 ft]; Profile1_Height=240 mm; Profile1_Length=46 mm; Profile1_Length_2=31 mm  [stored 0.101706 ft]; Profile_Dia=10 mm  [stored 0.0328084 ft]; Profile_Dia_2=10 mm  [stored 0.0328084 ft]; Profile_Dia_3=20 mm  [stored 0.0656168 ft]; Profile_height ref=45 mm; T_Height=233 mm; T_Height_2=200 mm; T_Height_Ref_1=33 mm; T_Height_Ref_2=39 mm  [stored 0.127953 ft]; Top_Profile=277 mm; Top_Profile_Ref=282 mm; W=410 mm; W_Ref=400 mm
- 879-0250-00-04400559999_DN250_PN10: Body_Collar_Dia=56 mm; Body_Collar_Dia_2=37 mm; Body_Flange_Dia=209 mm; Body_Flange_Dia_2=221 mm; Body_Height_1=209 mm; Body_Height_2=91 mm; Body_Height_3=81 mm; Body_Height_4=106 mm; Body_Top_Dia=24 mm  [stored 0.0787402 ft]; Body_Top_Dia_2=20 mm  [stored 0.0656168 ft]; Body_With_Dia=146 mm; Body_With_Dia_1=183 mm; Body_With_Dia_2=183 mm; Bolt_support=562 mm; Bolt_support_2=281 mm; Bolt_support_Dia=20 mm  [stored 0.0656168 ft]; Bolt_support_lenght=145 mm; Bolt_support_lenght_2=155 mm; Bottom_profile=63 mm; D1=160 mm; D3=198 mm; DN=250 mm; Fillet_Length=10 mm  [stored 0.0328084 ft]; Fillet_Length_2=40 mm  [stored 0.131234 ft]; Flange_thickness=22 mm  [stored 0.0721785 ft]; H3=706 mm; H3_Ref=660 mm; H3_Ref_2=335 mm; ID=125 mm; L=730 mm; PG_Dia=83 mm; PG_Ref=139 mm; PG_depth=14 mm  [stored 0.0459318 ft]; PG_height=446 mm; PG_height_1=404 mm; PG_ref=135 mm; PR_1=43 mm  [stored 0.141076 ft]; P_lenght=101 mm; Pilot_Dia_1=46 mm; Pilot_Dia_2=92 mm; Pilot_Dia_3=31 mm  [stored 0.101706 ft]; Pilot_Dia_4=15 mm  [stored 0.0492126 ft]; Pilot_Dia_5=10 mm  [stored 0.0328084 ft]; Pilot_top_1=452 mm; Pilot_top_ref=46 mm; Profile1_Height=275 mm; Profile1_Length=53 mm; Profile1_Length_2=36 mm  [stored 0.11811 ft]; Profile_Dia=10 mm  [stored 0.0328084 ft]; Profile_Dia_2=10 mm  [stored 0.0328084 ft]; Profile_Dia_3=20 mm  [stored 0.0656168 ft]; Profile_height ref=45 mm; T_Height=189 mm; T_Height_2=162 mm; T_Height_Ref_1=27 mm; T_Height_Ref_2=31 mm  [stored 0.101706 ft]; Top_Profile=337 mm; Top_Profile_Ref=342 mm; W=510 mm; W_Ref=500 mm
- 879-0250-00-044005599A0_DN250_PN10: Body_Collar_Dia=56 mm; Body_Collar_Dia_2=37 mm; Body_Flange_Dia=209 mm; Body_Flange_Dia_2=221 mm; Body_Height_1=209 mm; Body_Height_2=91 mm; Body_Height_3=160 mm; Body_Height_4=106 mm; Body_Top_Dia=24 mm  [stored 0.0787402 ft]; Body_Top_Dia_2=20 mm  [stored 0.0656168 ft]; Body_With_Dia=146 mm; Body_With_Dia_1=183 mm; Body_With_Dia_2=183 mm; Bolt_support=562 mm; Bolt_support_2=281 mm; Bolt_support_Dia=20 mm  [stored 0.0656168 ft]; Bolt_support_lenght=145 mm; Bolt_support_lenght_2=155 mm; Bottom_profile=63 mm; D1=160 mm; D3=198 mm; DN=250 mm; Fillet_Length=10 mm  [stored 0.0328084 ft]; Fillet_Length_2=40 mm  [stored 0.131234 ft]; Flange_thickness=22 mm  [stored 0.0721785 ft]; H3=806 mm; H3_Ref=749 mm; H3_Ref_2=335 mm; ID=125 mm; L=730 mm; PG_Dia=83 mm; PG_Ref=139 mm; PG_depth=14 mm  [stored 0.0459318 ft]; PG_height=484 mm; PG_height_1=442 mm; PG_ref=135 mm; PR_1=61 mm; P_lenght=101 mm; Pilot_Dia_1=46 mm; Pilot_Dia_2=92 mm; Pilot_Dia_3=31 mm  [stored 0.101706 ft]; Pilot_Dia_4=15 mm  [stored 0.0492126 ft]; Pilot_Dia_5=10 mm  [stored 0.0328084 ft]; Pilot_top_1=542 mm; Pilot_top_ref=57 mm; Profile1_Height=295 mm; Profile1_Length=53 mm; Profile1_Length_2=36 mm  [stored 0.11811 ft]; Profile_Dia=10 mm  [stored 0.0328084 ft]; Profile_Dia_2=10 mm  [stored 0.0328084 ft]; Profile_Dia_3=20 mm  [stored 0.0656168 ft]; Profile_height ref=45 mm; T_Height=269 mm; T_Height_2=230 mm; T_Height_Ref_1=38 mm; T_Height_Ref_2=45 mm; Top_Profile=337 mm; Top_Profile_Ref=342 mm; W=510 mm; W_Ref=500 mm
- 879-0250-00-14400559999_DN250_PN16: Body_Collar_Dia=56 mm; Body_Collar_Dia_2=37 mm; Body_Flange_Dia=209 mm; Body_Flange_Dia_2=221 mm; Body_Height_1=209 mm; Body_Height_2=91 mm; Body_Height_3=81 mm; Body_Height_4=106 mm; Body_Top_Dia=24 mm  [stored 0.0787402 ft]; Body_Top_Dia_2=20 mm  [stored 0.0656168 ft]; Body_With_Dia=146 mm; Body_With_Dia_1=183 mm; Body_With_Dia_2=183 mm; Bolt_support=562 mm; Bolt_support_2=281 mm; Bolt_support_Dia=20 mm  [stored 0.0656168 ft]; Bolt_support_lenght=145 mm; Bolt_support_lenght_2=155 mm; Bottom_profile=63 mm; D1=160 mm; D3=203 mm; DN=250 mm; Fillet_Length=10 mm  [stored 0.0328084 ft]; Fillet_Length_2=40 mm  [stored 0.131234 ft]; Flange_thickness=22 mm  [stored 0.0721785 ft]; H3=706 mm; H3_Ref=662 mm; H3_Ref_2=335 mm; ID=125 mm; L=730 mm; PG_Dia=83 mm; PG_Ref=139 mm; PG_depth=14 mm  [stored 0.0459318 ft]; PG_height=437 mm; PG_height_1=395 mm; PG_ref=135 mm; PR_1=44 mm; P_lenght=103 mm; Pilot_Dia_1=47 mm; Pilot_Dia_2=94 mm; Pilot_Dia_3=31 mm  [stored 0.101706 ft]; Pilot_Dia_4=16 mm  [stored 0.0524934 ft]; Pilot_Dia_5=10 mm  [stored 0.0328084 ft]; Pilot_top_1=450 mm; Pilot_top_ref=44 mm; Profile1_Height=265 mm; Profile1_Length=55 mm; Profile1_Length_2=36 mm  [stored 0.11811 ft]; Profile_Dia=10 mm  [stored 0.0328084 ft]; Profile_Dia_2=10 mm  [stored 0.0328084 ft]; Profile_Dia_3=20 mm  [stored 0.0656168 ft]; Profile_height ref=45 mm; T_Height=194 mm; T_Height_2=166 mm; T_Height_Ref_1=28 mm  [stored 0.0918635 ft]; T_Height_Ref_2=32 mm  [stored 0.104987 ft]; Top_Profile=337 mm; Top_Profile_Ref=342 mm; W=510 mm; W_Ref=500 mm
- 879-0250-00-144005599A0_DN250_PN16: Body_Collar_Dia=56 mm; Body_Collar_Dia_2=37 mm; Body_Flange_Dia=209 mm; Body_Flange_Dia_2=221 mm; Body_Height_1=209 mm; Body_Height_2=91 mm; Body_Height_3=155 mm; Body_Height_4=106 mm; Body_Top_Dia=24 mm  [stored 0.0787402 ft]; Body_Top_Dia_2=20 mm  [stored 0.0656168 ft]; Body_With_Dia=146 mm; Body_With_Dia_1=183 mm; Body_With_Dia_2=183 mm; Bolt_support=562 mm; Bolt_support_2=281 mm; Bolt_support_Dia=20 mm  [stored 0.0656168 ft]; Bolt_support_lenght=145 mm; Bolt_support_lenght_2=155 mm; Bottom_profile=63 mm; D1=160 mm; D3=203 mm; DN=250 mm; Fillet_Length=10 mm  [stored 0.0328084 ft]; Fillet_Length_2=40 mm  [stored 0.131234 ft]; Flange_thickness=22 mm  [stored 0.0721785 ft]; H3=806 mm; H3_Ref=749 mm; H3_Ref_2=335 mm; ID=125 mm; L=730 mm; PG_Dia=83 mm; PG_Ref=139 mm; PG_depth=14 mm  [stored 0.0459318 ft]; PG_height=468 mm; PG_height_1=426 mm; PG_ref=135 mm; PR_1=64 mm; P_lenght=103 mm; Pilot_Dia_1=47 mm; Pilot_Dia_2=94 mm; Pilot_Dia_3=31 mm  [stored 0.101706 ft]; Pilot_Dia_4=16 mm  [stored 0.0524934 ft]; Pilot_Dia_5=10 mm  [stored 0.0328084 ft]; Pilot_top_1=537 mm; Pilot_top_ref=57 mm; Profile1_Height=275 mm; Profile1_Length=55 mm; Profile1_Length_2=36 mm  [stored 0.11811 ft]; Profile_Dia=10 mm  [stored 0.0328084 ft]; Profile_Dia_2=10 mm  [stored 0.0328084 ft]; Profile_Dia_3=20 mm  [stored 0.0656168 ft]; Profile_height ref=45 mm; T_Height=284 mm; T_Height_2=243 mm; T_Height_Ref_1=41 mm  [stored 0.134514 ft]; T_Height_Ref_2=47 mm; Top_Profile=337 mm; Top_Profile_Ref=342 mm; W=510 mm; W_Ref=500 mm
- 879-0300-00-04400559999_DN300_PN10: Body_Collar_Dia=65 mm; Body_Collar_Dia_2=43 mm  [stored 0.141076 ft]; Body_Flange_Dia=243 mm; Body_Flange_Dia_2=258 mm; Body_Height_1=243 mm; Body_Height_2=106 mm; Body_Height_3=95 mm; Body_Height_4=121 mm; Body_Top_Dia=28 mm  [stored 0.0918635 ft]; Body_Top_Dia_2=24 mm  [stored 0.0787402 ft]; Body_With_Dia=170 mm; Body_With_Dia_1=213 mm; Body_With_Dia_2=213 mm; Bolt_support=654 mm; Bolt_support_2=327 mm; Bolt_support_Dia=20 mm  [stored 0.0656168 ft]; Bolt_support_lenght=170 mm; Bolt_support_lenght_2=180 mm; Bottom_profile=75 mm; D1=185 mm; D3=223 mm; DN=300 mm; Fillet_Length=10 mm  [stored 0.0328084 ft]; Fillet_Length_2=40 mm  [stored 0.131234 ft]; Flange_thickness=25 mm  [stored 0.082021 ft]; H3=782 mm; H3_Ref=742 mm; H3_Ref_2=384 mm; ID=150 mm; L=850 mm; PG_Dia=100 mm; PG_Ref=162 mm; PG_depth=14 mm  [stored 0.0459318 ft]; PG_height=513 mm; PG_height_1=463 mm; PG_ref=160 mm; PR_1=43 mm  [stored 0.141076 ft]; P_lenght=116 mm; Pilot_Dia_1=53 mm; Pilot_Dia_2=105 mm; Pilot_Dia_3=35 mm  [stored 0.114829 ft]; Pilot_Dia_4=18 mm; Pilot_Dia_5=12 mm  [stored 0.0393701 ft]; Pilot_top_1=509 mm; Pilot_top_ref=40 mm  [stored 0.131234 ft]; Profile1_Height=325 mm; Profile1_Length=60 mm; Profile1_Length_2=40 mm  [stored 0.131234 ft]; Profile_Dia=10 mm  [stored 0.0328084 ft]; Profile_Dia_2=10 mm  [stored 0.0328084 ft]; Profile_Dia_3=20 mm  [stored 0.0656168 ft]; Profile_height ref=45 mm; T_Height=190 mm; T_Height_2=162 mm; T_Height_Ref_1=27 mm; T_Height_Ref_2=32 mm  [stored 0.104987 ft]; Top_Profile=392 mm; Top_Profile_Ref=397 mm; W=555 mm; W_Ref=545 mm
- 879-0300-00-044005599A0_DN300_PN10: Body_Collar_Dia=65 mm; Body_Collar_Dia_2=43 mm  [stored 0.141076 ft]; Body_Flange_Dia=243 mm; Body_Flange_Dia_2=258 mm; Body_Height_1=243 mm; Body_Height_2=106 mm; Body_Height_3=140 mm; Body_Height_4=121 mm; Body_Top_Dia=28 mm  [stored 0.0918635 ft]; Body_Top_Dia_2=24 mm  [stored 0.0787402 ft]; Body_With_Dia=170 mm; Body_With_Dia_1=213 mm; Body_With_Dia_2=213 mm; Bolt_support=654 mm; Bolt_support_2=327 mm; Bolt_support_Dia=20 mm  [stored 0.0656168 ft]; Bolt_support_lenght=170 mm; Bolt_support_lenght_2=180 mm; Bottom_profile=75 mm; D1=185 mm; D3=223 mm; DN=300 mm; Fillet_Length=10 mm  [stored 0.0328084 ft]; Fillet_Length_2=40 mm  [stored 0.131234 ft]; Flange_thickness=25 mm  [stored 0.082021 ft]; H3=881 mm; H3_Ref=814 mm; H3_Ref_2=384 mm; ID=150 mm; L=850 mm; PG_Dia=100 mm; PG_Ref=162 mm; PG_depth=14 mm  [stored 0.0459318 ft]; PG_height=543 mm; PG_height_1=493 mm; PG_ref=160 mm; PR_1=63 mm; P_lenght=116 mm; Pilot_Dia_1=53 mm; Pilot_Dia_2=105 mm; Pilot_Dia_3=35 mm  [stored 0.114829 ft]; Pilot_Dia_4=18 mm; Pilot_Dia_5=12 mm  [stored 0.0393701 ft]; Pilot_top_1=581 mm; Pilot_top_ref=67 mm; Profile1_Height=335 mm; Profile1_Length=60 mm; Profile1_Length_2=40 mm  [stored 0.131234 ft]; Profile_Dia=10 mm  [stored 0.0328084 ft]; Profile_Dia_2=10 mm  [stored 0.0328084 ft]; Profile_Dia_3=20 mm  [stored 0.0656168 ft]; Profile_height ref=45 mm; T_Height=279 mm; T_Height_2=239 mm; T_Height_Ref_1=40 mm  [stored 0.131234 ft]; T_Height_Ref_2=46 mm; Top_Profile=392 mm; Top_Profile_Ref=397 mm; W=555 mm; W_Ref=545 mm
- 879-0300-00-14400559999_DN300_PN16: Body_Collar_Dia=65 mm; Body_Collar_Dia_2=43 mm  [stored 0.141076 ft]; Body_Flange_Dia=243 mm; Body_Flange_Dia_2=258 mm; Body_Height_1=243 mm; Body_Height_2=106 mm; Body_Height_3=95 mm; Body_Height_4=121 mm; Body_Top_Dia=28 mm  [stored 0.0918635 ft]; Body_Top_Dia_2=24 mm  [stored 0.0787402 ft]; Body_With_Dia=170 mm; Body_With_Dia_1=213 mm; Body_With_Dia_2=213 mm; Bolt_support=654 mm; Bolt_support_2=327 mm; Bolt_support_Dia=20 mm  [stored 0.0656168 ft]; Bolt_support_lenght=170 mm; Bolt_support_lenght_2=180 mm; Bottom_profile=75 mm; D1=185 mm; D3=230 mm; DN=300 mm; Fillet_Length=10 mm  [stored 0.0328084 ft]; Fillet_Length_2=40 mm  [stored 0.131234 ft]; Flange_thickness=25 mm  [stored 0.082021 ft]; H3=782 mm; H3_Ref=745 mm; H3_Ref_2=384 mm; ID=150 mm; L=850 mm; PG_Dia=100 mm; PG_Ref=162 mm; PG_depth=14 mm  [stored 0.0459318 ft]; PG_height=511 mm; PG_height_1=461 mm; PG_ref=160 mm; PR_1=41 mm  [stored 0.134514 ft]; P_lenght=120 mm; Pilot_Dia_1=55 mm; Pilot_Dia_2=109 mm; Pilot_Dia_3=36 mm  [stored 0.11811 ft]; Pilot_Dia_4=18 mm; Pilot_Dia_5=12 mm  [stored 0.0393701 ft]; Pilot_top_1=505 mm; Pilot_top_ref=37 mm; Profile1_Height=325 mm; Profile1_Length=62 mm; Profile1_Length_2=41 mm  [stored 0.134514 ft]; Profile_Dia=10 mm  [stored 0.0328084 ft]; Profile_Dia_2=10 mm  [stored 0.0328084 ft]; Profile_Dia_3=20 mm  [stored 0.0656168 ft]; Profile_height ref=45 mm; T_Height=182 mm; T_Height_2=156 mm; T_Height_Ref_1=26 mm; T_Height_Ref_2=30 mm  [stored 0.0984252 ft]; Top_Profile=392 mm; Top_Profile_Ref=397 mm; W=555 mm; W_Ref=545 mm
- 879-0300-00-144005599A0_DN300_PN16: Body_Collar_Dia=65 mm; Body_Collar_Dia_2=43 mm  [stored 0.141076 ft]; Body_Flange_Dia=243 mm; Body_Flange_Dia_2=258 mm; Body_Height_1=243 mm; Body_Height_2=106 mm; Body_Height_3=130 mm; Body_Height_4=121 mm; Body_Top_Dia=28 mm  [stored 0.0918635 ft]; Body_Top_Dia_2=24 mm  [stored 0.0787402 ft]; Body_With_Dia=170 mm; Body_With_Dia_1=213 mm; Body_With_Dia_2=213 mm; Bolt_support=654 mm; Bolt_support_2=327 mm; Bolt_support_Dia=20 mm  [stored 0.0656168 ft]; Bolt_support_lenght=170 mm; Bolt_support_lenght_2=180 mm; Bottom_profile=75 mm; D1=185 mm; D3=230 mm; DN=300 mm; Fillet_Length=10 mm  [stored 0.0328084 ft]; Fillet_Length_2=40 mm  [stored 0.131234 ft]; Flange_thickness=25 mm  [stored 0.082021 ft]; H3=881 mm; H3_Ref=813 mm; H3_Ref_2=384 mm; ID=150 mm; L=850 mm; PG_Dia=100 mm; PG_Ref=162 mm; PG_depth=14 mm  [stored 0.0459318 ft]; PG_height=534 mm; PG_height_1=484 mm; PG_ref=160 mm; PR_1=64 mm; P_lenght=120 mm; Pilot_Dia_1=55 mm; Pilot_Dia_2=109 mm; Pilot_Dia_3=36 mm  [stored 0.11811 ft]; Pilot_Dia_4=18 mm; Pilot_Dia_5=12 mm  [stored 0.0393701 ft]; Pilot_top_1=573 mm; Pilot_top_ref=68 mm; Profile1_Height=325 mm; Profile1_Length=62 mm; Profile1_Length_2=41 mm  [stored 0.134514 ft]; Profile_Dia=10 mm  [stored 0.0328084 ft]; Profile_Dia_2=10 mm  [stored 0.0328084 ft]; Profile_Dia_3=20 mm  [stored 0.0656168 ft]; Profile_height ref=45 mm; T_Height=281 mm; T_Height_2=241 mm; T_Height_Ref_1=40 mm  [stored 0.131234 ft]; T_Height_Ref_2=47 mm; Top_Profile=392 mm; Top_Profile_Ref=397 mm; W=555 mm; W_Ref=545 mm
- 879-0350-00-04400559999_DN350_PN10: Body_Collar_Dia=75 mm; Body_Collar_Dia_2=49 mm; Body_Flange_Dia=280 mm; Body_Flange_Dia_2=297 mm; Body_Height_1=280 mm; Body_Height_2=123 mm; Body_Height_3=98 mm; Body_Height_4=138 mm; Body_Top_Dia=33 mm; Body_Top_Dia_2=27 mm; Body_With_Dia=196 mm; Body_With_Dia_1=245 mm; Body_With_Dia_2=245 mm; Bolt_support=754 mm; Bolt_support_2=377 mm; Bolt_support_Dia=30 mm  [stored 0.0984252 ft]; Bolt_support_lenght=195 mm; Bolt_support_lenght_2=205 mm; Bottom_profile=88 mm; D1=215 mm; D3=253 mm; DN=350 mm; Fillet_Length=15 mm  [stored 0.0492126 ft]; Fillet_Length_2=60 mm; Flange_thickness=27 mm; H3=872 mm; H3_Ref=830 mm; H3_Ref_2=438 mm; ID=175 mm; L=980 mm; PG_Dia=117 mm; PG_Ref=187 mm; PG_depth=21 mm  [stored 0.0688976 ft]; PG_height=578 mm; PG_height_1=520 mm; PG_ref=185 mm; PR_1=46 mm; P_lenght=133 mm; Pilot_Dia_1=61 mm; Pilot_Dia_2=121 mm; Pilot_Dia_3=40 mm  [stored 0.131234 ft]; Pilot_Dia_4=20 mm  [stored 0.0656168 ft]; Pilot_Dia_5=13 mm  [stored 0.0426509 ft]; Pilot_top_1=568 mm; Pilot_top_ref=42 mm  [stored 0.137795 ft]; Profile1_Height=365 mm; Profile1_Length=68 mm; Profile1_Length_2=45 mm; Profile_Dia=15 mm  [stored 0.0492126 ft]; Profile_Dia_2=15 mm  [stored 0.0492126 ft]; Profile_Dia_3=30 mm  [stored 0.0984252 ft]; Profile_height ref=50 mm; T_Height=205 mm; T_Height_2=175 mm; T_Height_Ref_1=29 mm; T_Height_Ref_2=34 mm; Top_Profile=452 mm; Top_Profile_Ref=457 mm; W=605 mm; W_Ref=590 mm
- 879-0350-00-044005599A0_DN350_PN10: Body_Collar_Dia=75 mm; Body_Collar_Dia_2=49 mm; Body_Flange_Dia=280 mm; Body_Flange_Dia_2=297 mm; Body_Height_1=280 mm; Body_Height_2=123 mm; Body_Height_3=155 mm; Body_Height_4=138 mm; Body_Top_Dia=33 mm; Body_Top_Dia_2=27 mm; Body_With_Dia=196 mm; Body_With_Dia_1=245 mm; Body_With_Dia_2=245 mm; Bolt_support=754 mm; Bolt_support_2=377 mm; Bolt_support_Dia=30 mm  [stored 0.0984252 ft]; Bolt_support_lenght=195 mm; Bolt_support_lenght_2=205 mm; Bottom_profile=88 mm; D1=215 mm; D3=253 mm; DN=350 mm; Fillet_Length=15 mm  [stored 0.0492126 ft]; Fillet_Length_2=60 mm; Flange_thickness=27 mm; H3=959 mm; H3_Ref=902 mm; H3_Ref_2=438 mm; ID=175 mm; L=980 mm; PG_Dia=117 mm; PG_Ref=187 mm; PG_depth=21 mm  [stored 0.0688976 ft]; PG_height=598 mm; PG_height_1=539 mm; PG_ref=185 mm; PR_1=66 mm; P_lenght=133 mm; Pilot_Dia_1=61 mm; Pilot_Dia_2=121 mm; Pilot_Dia_3=40 mm  [stored 0.131234 ft]; Pilot_Dia_4=20 mm  [stored 0.0656168 ft]; Pilot_Dia_5=13 mm  [stored 0.0426509 ft]; Pilot_top_1=640 mm; Pilot_top_ref=57 mm; Profile1_Height=365 mm; Profile1_Length=68 mm; Profile1_Length_2=45 mm; Profile_Dia=15 mm  [stored 0.0492126 ft]; Profile_Dia_2=15 mm  [stored 0.0492126 ft]; Profile_Dia_3=30 mm  [stored 0.0984252 ft]; Profile_height ref=50 mm; T_Height=292 mm; T_Height_2=250 mm; T_Height_Ref_1=42 mm  [stored 0.137795 ft]; T_Height_Ref_2=49 mm; Top_Profile=452 mm; Top_Profile_Ref=457 mm; W=605 mm; W_Ref=590 mm
- 879-0350-00-14400559999_DN350_PN16: Body_Collar_Dia=75 mm; Body_Collar_Dia_2=49 mm; Body_Flange_Dia=280 mm; Body_Flange_Dia_2=297 mm; Body_Height_1=280 mm; Body_Height_2=123 mm; Body_Height_3=89 mm; Body_Height_4=138 mm; Body_Top_Dia=33 mm; Body_Top_Dia_2=27 mm; Body_With_Dia=196 mm; Body_With_Dia_1=245 mm; Body_With_Dia_2=245 mm; Bolt_support=754 mm; Bolt_support_2=377 mm; Bolt_support_Dia=30 mm  [stored 0.0984252 ft]; Bolt_support_lenght=195 mm; Bolt_support_lenght_2=205 mm; Bottom_profile=88 mm; D1=215 mm; D3=260 mm; DN=350 mm; Fillet_Length=15 mm  [stored 0.0492126 ft]; Fillet_Length_2=60 mm; Flange_thickness=27 mm; H3=872 mm; H3_Ref=829 mm; H3_Ref_2=438 mm; ID=175 mm; L=980 mm; PG_Dia=117 mm; PG_Ref=187 mm; PG_depth=21 mm  [stored 0.0688976 ft]; PG_height=569 mm; PG_height_1=510 mm; PG_ref=185 mm; PR_1=47 mm; P_lenght=139 mm; Pilot_Dia_1=63 mm; Pilot_Dia_2=126 mm; Pilot_Dia_3=42 mm  [stored 0.137795 ft]; Pilot_Dia_4=21 mm  [stored 0.0688976 ft]; Pilot_Dia_5=14 mm  [stored 0.0459318 ft]; Pilot_top_1=559 mm; Pilot_top_ref=43 mm  [stored 0.141076 ft]; Profile1_Height=355 mm; Profile1_Length=70 mm; Profile1_Length_2=47 mm; Profile_Dia=15 mm  [stored 0.0492126 ft]; Profile_Dia_2=15 mm  [stored 0.0492126 ft]; Profile_Dia_3=30 mm  [stored 0.0984252 ft]; Profile_height ref=50 mm; T_Height=207 mm; T_Height_2=177 mm; T_Height_Ref_1=30 mm  [stored 0.0984252 ft]; T_Height_Ref_2=35 mm  [stored 0.114829 ft]; Top_Profile=452 mm; Top_Profile_Ref=457 mm; W=605 mm; W_Ref=590 mm
- 879-0350-00-144005599A0_DN350_PN16: Body_Collar_Dia=75 mm; Body_Collar_Dia_2=49 mm; Body_Flange_Dia=280 mm; Body_Flange_Dia_2=297 mm; Body_Height_1=280 mm; Body_Height_2=123 mm; Body_Height_3=150 mm; Body_Height_4=138 mm; Body_Top_Dia=33 mm; Body_Top_Dia_2=27 mm; Body_With_Dia=196 mm; Body_With_Dia_1=245 mm; Body_With_Dia_2=245 mm; Bolt_support=754 mm; Bolt_support_2=377 mm; Bolt_support_Dia=30 mm  [stored 0.0984252 ft]; Bolt_support_lenght=195 mm; Bolt_support_lenght_2=205 mm; Bottom_profile=88 mm; D1=215 mm; D3=260 mm; DN=350 mm; Fillet_Length=15 mm  [stored 0.0492126 ft]; Fillet_Length_2=60 mm; Flange_thickness=27 mm; H3=959 mm; H3_Ref=903 mm; H3_Ref_2=438 mm; ID=175 mm; L=980 mm; PG_Dia=117 mm; PG_Ref=187 mm; PG_depth=21 mm  [stored 0.0688976 ft]; PG_height=588 mm; PG_height_1=530 mm; PG_ref=185 mm; PR_1=67 mm; P_lenght=139 mm; Pilot_Dia_1=63 mm; Pilot_Dia_2=126 mm; Pilot_Dia_3=42 mm  [stored 0.137795 ft]; Pilot_Dia_4=21 mm  [stored 0.0688976 ft]; Pilot_Dia_5=14 mm  [stored 0.0459318 ft]; Pilot_top_1=633 mm; Pilot_top_ref=56 mm; Profile1_Height=355 mm; Profile1_Length=70 mm; Profile1_Length_2=47 mm; Profile_Dia=15 mm  [stored 0.0492126 ft]; Profile_Dia_2=15 mm  [stored 0.0492126 ft]; Profile_Dia_3=30 mm  [stored 0.0984252 ft]; Profile_height ref=50 mm; T_Height=294 mm; T_Height_2=252 mm; T_Height_Ref_1=42 mm  [stored 0.137795 ft]; T_Height_Ref_2=49 mm; Top_Profile=452 mm; Top_Profile_Ref=457 mm; W=605 mm; W_Ref=590 mm
- 879-0400-00-04400559999_DN400_PN10: Body_Collar_Dia=85 mm; Body_Collar_Dia_2=55 mm; Body_Flange_Dia=314 mm; Body_Flange_Dia_2=333 mm; Body_Height_1=314 mm; Body_Height_2=138 mm; Body_Height_3=110 mm; Body_Height_4=153 mm; Body_Top_Dia=37 mm; Body_Top_Dia_2=31 mm  [stored 0.101706 ft]; Body_With_Dia=220 mm; Body_With_Dia_1=275 mm; Body_With_Dia_2=275 mm; Bolt_support=846 mm; Bolt_support_2=423 mm; Bolt_support_Dia=40 mm  [stored 0.131234 ft]; Bolt_support_lenght=220 mm; Bolt_support_lenght_2=230 mm; Bottom_profile=100 mm; D1=240 mm; D3=283 mm; DN=400 mm; Fillet_Length=20 mm  [stored 0.0656168 ft]; Fillet_Length_2=80 mm; Flange_thickness=28 mm  [stored 0.0918635 ft]; H3=996 mm; H3_Ref=938 mm; H3_Ref_2=487 mm; ID=200 mm; L=1100 mm; PG_Dia=133 mm; PG_Ref=210 mm; PG_depth=28 mm  [stored 0.0918635 ft]; PG_height=643 mm; PG_height_1=576 mm; PG_ref=210 mm; PR_1=60 mm; P_lenght=152 mm; Pilot_Dia_1=69 mm; Pilot_Dia_2=138 mm; Pilot_Dia_3=46 mm; Pilot_Dia_4=23 mm  [stored 0.0754593 ft]; Pilot_Dia_5=15 mm  [stored 0.0492126 ft]; Pilot_top_1=645 mm; Pilot_top_ref=58 mm; Profile1_Height=395 mm; Profile1_Length=76 mm; Profile1_Length_2=51 mm; Profile_Dia=20 mm  [stored 0.0656168 ft]; Profile_Dia_2=20 mm  [stored 0.0656168 ft]; Profile_Dia_3=40 mm  [stored 0.131234 ft]; Profile_height ref=55 mm; T_Height=264 mm; T_Height_2=226 mm; T_Height_Ref_1=38 mm; T_Height_Ref_2=44 mm; Top_Profile=508 mm; Top_Profile_Ref=513 mm; W=710 mm; W_Ref=690 mm
- 879-0400-00-044005599A0_DN400_PN10: Body_Collar_Dia=85 mm; Body_Collar_Dia_2=55 mm; Body_Flange_Dia=314 mm; Body_Flange_Dia_2=333 mm; Body_Height_1=314 mm; Body_Height_2=138 mm; Body_Height_3=185 mm; Body_Height_4=153 mm; Body_Top_Dia=37 mm; Body_Top_Dia_2=31 mm  [stored 0.101706 ft]; Body_With_Dia=220 mm; Body_With_Dia_1=275 mm; Body_With_Dia_2=275 mm; Bolt_support=846 mm; Bolt_support_2=423 mm; Bolt_support_Dia=40 mm  [stored 0.131234 ft]; Bolt_support_lenght=220 mm; Bolt_support_lenght_2=230 mm; Bottom_profile=100 mm; D1=240 mm; D3=283 mm; DN=400 mm; Fillet_Length=20 mm  [stored 0.0656168 ft]; Fillet_Length_2=80 mm; Flange_thickness=28 mm  [stored 0.0918635 ft]; H3=1159 mm; H3_Ref=1057 mm; H3_Ref_2=487 mm; ID=200 mm; L=1100 mm; PG_Dia=133 mm; PG_Ref=210 mm; PG_depth=28 mm  [stored 0.0918635 ft]; PG_height=680 mm; PG_height_1=613 mm; PG_ref=210 mm; PR_1=96 mm; P_lenght=152 mm; Pilot_Dia_1=69 mm; Pilot_Dia_2=138 mm; Pilot_Dia_3=46 mm; Pilot_Dia_4=23 mm  [stored 0.0754593 ft]; Pilot_Dia_5=15 mm  [stored 0.0492126 ft]; Pilot_top_1=764 mm; Pilot_top_ref=102 mm; Profile1_Height=395 mm; Profile1_Length=76 mm; Profile1_Length_2=51 mm; Profile_Dia=20 mm  [stored 0.0656168 ft]; Profile_Dia_2=20 mm  [stored 0.0656168 ft]; Profile_Dia_3=40 mm  [stored 0.131234 ft]; Profile_height ref=55 mm; T_Height=427 mm; T_Height_2=366 mm; T_Height_Ref_1=61 mm; T_Height_Ref_2=71 mm; Top_Profile=508 mm; Top_Profile_Ref=513 mm; W=710 mm; W_Ref=690 mm
- 879-0400-00-14400559999_DN400_PN16: Body_Collar_Dia=85 mm; Body_Collar_Dia_2=55 mm; Body_Flange_Dia=314 mm; Body_Flange_Dia_2=333 mm; Body_Height_1=314 mm; Body_Height_2=138 mm; Body_Height_3=100 mm; Body_Height_4=153 mm; Body_Top_Dia=37 mm; Body_Top_Dia_2=31 mm  [stored 0.101706 ft]; Body_With_Dia=220 mm; Body_With_Dia_1=275 mm; Body_With_Dia_2=275 mm; Bolt_support=846 mm; Bolt_support_2=423 mm; Bolt_support_Dia=40 mm  [stored 0.131234 ft]; Bolt_support_lenght=220 mm; Bolt_support_lenght_2=230 mm; Bottom_profile=100 mm; D1=240 mm; D3=290 mm; DN=400 mm; Fillet_Length=20 mm  [stored 0.0656168 ft]; Fillet_Length_2=80 mm; Flange_thickness=28 mm  [stored 0.0918635 ft]; H3=996 mm; H3_Ref=936 mm; H3_Ref_2=487 mm; ID=200 mm; L=1100 mm; PG_Dia=133 mm; PG_Ref=210 mm; PG_depth=28 mm  [stored 0.0918635 ft]; PG_height=641 mm; PG_height_1=575 mm; PG_ref=210 mm; PR_1=58 mm; P_lenght=156 mm; Pilot_Dia_1=71 mm; Pilot_Dia_2=142 mm; Pilot_Dia_3=47 mm; Pilot_Dia_4=24 mm  [stored 0.0787402 ft]; Pilot_Dia_5=16 mm  [stored 0.0524934 ft]; Pilot_top_1=636 mm; Pilot_top_ref=60 mm; Profile1_Height=395 mm; Profile1_Length=78 mm; Profile1_Length_2=52 mm; Profile_Dia=20 mm  [stored 0.0656168 ft]; Profile_Dia_2=20 mm  [stored 0.0656168 ft]; Profile_Dia_3=40 mm  [stored 0.131234 ft]; Profile_height ref=55 mm; T_Height=256 mm; T_Height_2=219 mm; T_Height_Ref_1=37 mm; T_Height_Ref_2=43 mm  [stored 0.141076 ft]; Top_Profile=508 mm; Top_Profile_Ref=513 mm; W=710 mm; W_Ref=690 mm
- 879-0400-00-144005599A0_DN400_PN16: Body_Collar_Dia=85 mm; Body_Collar_Dia_2=55 mm; Body_Flange_Dia=314 mm; Body_Flange_Dia_2=333 mm; Body_Height_1=314 mm; Body_Height_2=138 mm; Body_Height_3=230 mm; Body_Height_4=153 mm; Body_Top_Dia=37 mm; Body_Top_Dia_2=31 mm  [stored 0.101706 ft]; Body_With_Dia=220 mm; Body_With_Dia_1=275 mm; Body_With_Dia_2=275 mm; Bolt_support=846 mm; Bolt_support_2=423 mm; Bolt_support_Dia=40 mm  [stored 0.131234 ft]; Bolt_support_lenght=220 mm; Bolt_support_lenght_2=230 mm; Bottom_profile=100 mm; D1=240 mm; D3=290 mm; DN=400 mm; Fillet_Length=20 mm  [stored 0.0656168 ft]; Fillet_Length_2=80 mm; Flange_thickness=28 mm  [stored 0.0918635 ft]; H3=1159 mm; H3_Ref=1083 mm; H3_Ref_2=487 mm; ID=200 mm; L=1100 mm; PG_Dia=133 mm; PG_Ref=210 mm; PG_depth=28 mm  [stored 0.0918635 ft]; PG_height=686 mm; PG_height_1=619 mm; PG_ref=210 mm; PR_1=93 mm; P_lenght=156 mm; Pilot_Dia_1=71 mm; Pilot_Dia_2=142 mm; Pilot_Dia_3=47 mm; Pilot_Dia_4=24 mm  [stored 0.0787402 ft]; Pilot_Dia_5=16 mm  [stored 0.0524934 ft]; Pilot_top_1=783 mm; Pilot_top_ref=76 mm; Profile1_Height=405 mm; Profile1_Length=78 mm; Profile1_Length_2=52 mm; Profile_Dia=20 mm  [stored 0.0656168 ft]; Profile_Dia_2=20 mm  [stored 0.0656168 ft]; Profile_Dia_3=40 mm  [stored 0.131234 ft]; Profile_height ref=55 mm; T_Height=409 mm; T_Height_2=351 mm; T_Height_Ref_1=58 mm; T_Height_Ref_2=68 mm; Top_Profile=508 mm; Top_Profile_Ref=513 mm; W=710 mm; W_Ref=690 mm
- 879-0450-00-04400559999_DN450_PN10: Body_Collar_Dia=92 mm; Body_Collar_Dia_2=60 mm; Body_Flange_Dia=343 mm; Body_Flange_Dia_2=364 mm; Body_Height_1=343 mm; Body_Height_2=150 mm; Body_Height_3=135 mm; Body_Height_4=165 mm; Body_Top_Dia=40 mm  [stored 0.131234 ft]; Body_Top_Dia_2=33 mm; Body_With_Dia=240 mm; Body_With_Dia_1=300 mm; Body_With_Dia_2=300 mm; Bolt_support=923 mm; Bolt_support_2=462 mm; Bolt_support_Dia=40 mm  [stored 0.131234 ft]; Bolt_support_lenght=245 mm; Bolt_support_lenght_2=255 mm; Bottom_profile=113 mm; D1=265 mm; D3=308 mm; DN=450 mm; Fillet_Length=20 mm  [stored 0.0656168 ft]; Fillet_Length_2=80 mm; Flange_thickness=30 mm  [stored 0.0984252 ft]; H3=1057 mm; H3_Ref=1014 mm; H3_Ref_2=528 mm; ID=225 mm; L=1200 mm; PG_Dia=150 mm; PG_Ref=229 mm; PG_depth=28 mm  [stored 0.0918635 ft]; PG_height=706 mm; PG_height_1=631 mm; PG_ref=235 mm; PR_1=56 mm; P_lenght=166 mm; Pilot_Dia_1=76 mm; Pilot_Dia_2=151 mm; Pilot_Dia_3=50 mm; Pilot_Dia_4=25 mm  [stored 0.082021 ft]; Pilot_Dia_5=17 mm; Pilot_top_1=696 mm; Pilot_top_ref=43 mm  [stored 0.141076 ft]; Profile1_Height=445 mm; Profile1_Length=83 mm; Profile1_Length_2=55 mm; Profile_Dia=20 mm  [stored 0.0656168 ft]; Profile_Dia_2=20 mm  [stored 0.0656168 ft]; Profile_Dia_3=40 mm  [stored 0.131234 ft]; Profile_height ref=55 mm; T_Height=250 mm; T_Height_2=214 mm; T_Height_Ref_1=36 mm  [stored 0.11811 ft]; T_Height_Ref_2=42 mm  [stored 0.137795 ft]; Top_Profile=554 mm; Top_Profile_Ref=559 mm; W=780 mm; W_Ref=760 mm
- 879-0450-00-044005599A0_DN450_PN10: Body_Collar_Dia=92 mm; Body_Collar_Dia_2=60 mm; Body_Flange_Dia=343 mm; Body_Flange_Dia_2=364 mm; Body_Height_1=343 mm; Body_Height_2=150 mm; Body_Height_3=260 mm; Body_Height_4=165 mm; Body_Top_Dia=40 mm  [stored 0.131234 ft]; Body_Top_Dia_2=33 mm; Body_With_Dia=240 mm; Body_With_Dia_1=300 mm; Body_With_Dia_2=300 mm; Bolt_support=923 mm; Bolt_support_2=462 mm; Bolt_support_Dia=40 mm  [stored 0.131234 ft]; Bolt_support_lenght=245 mm; Bolt_support_lenght_2=255 mm; Bottom_profile=113 mm; D1=265 mm; D3=308 mm; DN=450 mm; Fillet_Length=20 mm  [stored 0.0656168 ft]; Fillet_Length_2=80 mm; Flange_thickness=30 mm  [stored 0.0984252 ft]; H3=1220 mm; H3_Ref=1158 mm; H3_Ref_2=528 mm; ID=225 mm; L=1200 mm; PG_Dia=150 mm; PG_Ref=229 mm; PG_depth=28 mm  [stored 0.0918635 ft]; PG_height=743 mm; PG_height_1=668 mm; PG_ref=235 mm; PR_1=93 mm; P_lenght=166 mm; Pilot_Dia_1=76 mm; Pilot_Dia_2=151 mm; Pilot_Dia_3=50 mm; Pilot_Dia_4=25 mm  [stored 0.082021 ft]; Pilot_Dia_5=17 mm; Pilot_top_1=840 mm; Pilot_top_ref=62 mm; Profile1_Height=445 mm; Profile1_Length=83 mm; Profile1_Length_2=55 mm; Profile_Dia=20 mm  [stored 0.0656168 ft]; Profile_Dia_2=20 mm  [stored 0.0656168 ft]; Profile_Dia_3=40 mm  [stored 0.131234 ft]; Profile_height ref=55 mm; T_Height=413 mm; T_Height_2=354 mm; T_Height_Ref_1=59 mm; T_Height_Ref_2=69 mm; Top_Profile=554 mm; Top_Profile_Ref=559 mm; W=780 mm; W_Ref=760 mm
- 879-0450-00-14400559999_DN450_PN16: Body_Collar_Dia=92 mm; Body_Collar_Dia_2=60 mm; Body_Flange_Dia=343 mm; Body_Flange_Dia_2=364 mm; Body_Height_1=343 mm; Body_Height_2=150 mm; Body_Height_3=120 mm; Body_Height_4=165 mm; Body_Top_Dia=40 mm  [stored 0.131234 ft]; Body_Top_Dia_2=33 mm; Body_With_Dia=240 mm; Body_With_Dia_1=300 mm; Body_With_Dia_2=300 mm; Bolt_support=923 mm; Bolt_support_2=462 mm; Bolt_support_Dia=40 mm  [stored 0.131234 ft]; Bolt_support_lenght=245 mm; Bolt_support_lenght_2=255 mm; Bottom_profile=113 mm; D1=274 mm; D3=320 mm; DN=450 mm; Fillet_Length=20 mm  [stored 0.0656168 ft]; Fillet_Length_2=80 mm; Flange_thickness=30 mm  [stored 0.0984252 ft]; H3=1057 mm; H3_Ref=1012 mm; H3_Ref_2=528 mm; ID=225 mm; L=1200 mm; PG_Dia=150 mm; PG_Ref=229 mm; PG_depth=28 mm  [stored 0.0918635 ft]; PG_height=704 mm; PG_height_1=629 mm; PG_ref=235 mm; PR_1=54 mm; P_lenght=174 mm; Pilot_Dia_1=79 mm; Pilot_Dia_2=158 mm; Pilot_Dia_3=53 mm; Pilot_Dia_4=26 mm; Pilot_Dia_5=18 mm; Pilot_top_1=682 mm; Pilot_top_ref=45 mm; Profile1_Height=445 mm; Profile1_Length=86 mm; Profile1_Length_2=58 mm; Profile_Dia=20 mm  [stored 0.0656168 ft]; Profile_Dia_2=20 mm  [stored 0.0656168 ft]; Profile_Dia_3=40 mm  [stored 0.131234 ft]; Profile_height ref=55 mm; T_Height=237 mm; T_Height_2=203 mm; T_Height_Ref_1=34 mm; T_Height_Ref_2=40 mm  [stored 0.131234 ft]; Top_Profile=554 mm; Top_Profile_Ref=559 mm; W=780 mm; W_Ref=760 mm
- 879-0450-00-144005599A0_DN450_PN16: Body_Collar_Dia=92 mm; Body_Collar_Dia_2=60 mm; Body_Flange_Dia=343 mm; Body_Flange_Dia_2=364 mm; Body_Height_1=343 mm; Body_Height_2=150 mm; Body_Height_3=260 mm; Body_Height_4=165 mm; Body_Top_Dia=40 mm  [stored 0.131234 ft]; Body_Top_Dia_2=33 mm; Body_With_Dia=240 mm; Body_With_Dia_1=300 mm; Body_With_Dia_2=300 mm; Bolt_support=923 mm; Bolt_support_2=462 mm; Bolt_support_Dia=40 mm  [stored 0.131234 ft]; Bolt_support_lenght=245 mm; Bolt_support_lenght_2=255 mm; Bottom_profile=113 mm; D1=274 mm; D3=320 mm; DN=450 mm; Fillet_Length=20 mm  [stored 0.0656168 ft]; Fillet_Length_2=80 mm; Flange_thickness=30 mm  [stored 0.0984252 ft]; H3=1220 mm; H3_Ref=1164 mm; H3_Ref_2=528 mm; ID=225 mm; L=1200 mm; PG_Dia=150 mm; PG_Ref=229 mm; PG_depth=28 mm  [stored 0.0918635 ft]; PG_height=741 mm; PG_height_1=666 mm; PG_ref=235 mm; PR_1=90 mm; P_lenght=174 mm; Pilot_Dia_1=79 mm; Pilot_Dia_2=158 mm; Pilot_Dia_3=53 mm; Pilot_Dia_4=26 mm; Pilot_Dia_5=18 mm; Pilot_top_1=834 mm; Pilot_top_ref=56 mm; Profile1_Height=445 mm; Profile1_Length=86 mm; Profile1_Length_2=58 mm; Profile_Dia=20 mm  [stored 0.0656168 ft]; Profile_Dia_2=20 mm  [stored 0.0656168 ft]; Profile_Dia_3=40 mm  [stored 0.131234 ft]; Profile_height ref=55 mm; T_Height=400 mm; T_Height_2=343 mm; T_Height_Ref_1=57 mm; T_Height_Ref_2=67 mm; Top_Profile=554 mm; Top_Profile_Ref=559 mm; W=780 mm; W_Ref=760 mm
- 879-0500-00-04400559999_DN500_PN10: Body_Collar_Dia=96 mm; Body_Collar_Dia_2=63 mm; Body_Flange_Dia=357 mm; Body_Flange_Dia_2=379 mm; Body_Height_1=357 mm; Body_Height_2=156 mm; Body_Height_3=200 mm; Body_Height_4=171 mm; Body_Top_Dia=42 mm  [stored 0.137795 ft]; Body_Top_Dia_2=35 mm  [stored 0.114829 ft]; Body_With_Dia=250 mm; Body_With_Dia_1=313 mm; Body_With_Dia_2=313 mm; Bolt_support=962 mm; Bolt_support_2=481 mm; Bolt_support_Dia=50 mm; Bolt_support_lenght=270 mm; Bolt_support_lenght_2=280 mm; Bottom_profile=125 mm; D1=291 mm; D3=335 mm; DN=500 mm; Fillet_Length=25 mm  [stored 0.082021 ft]; Fillet_Length_2=100 mm; Flange_thickness=32 mm  [stored 0.104987 ft]; H3=1245 mm; H3_Ref=1164 mm; H3_Ref_2=548 mm; ID=250 mm; L=1250 mm; PG_Dia=167 mm; PG_Ref=238 mm; PG_depth=35 mm  [stored 0.114829 ft]; PG_height=767 mm; PG_height_1=684 mm; PG_ref=260 mm; PR_1=90 mm; P_lenght=183 mm; Pilot_Dia_1=83 mm; Pilot_Dia_2=166 mm; Pilot_Dia_3=55 mm; Pilot_Dia_4=28 mm  [stored 0.0918635 ft]; Pilot_Dia_5=18 mm; Pilot_top_1=819 mm; Pilot_top_ref=81 mm; Profile1_Height=450 mm; Profile1_Length=91 mm; Profile1_Length_2=60 mm; Profile_Dia=25 mm  [stored 0.082021 ft]; Profile_Dia_2=25 mm  [stored 0.082021 ft]; Profile_Dia_3=50 mm; Profile_height ref=60 mm; T_Height=400 mm; T_Height_2=343 mm; T_Height_Ref_1=57 mm; T_Height_Ref_2=67 mm; Top_Profile=577 mm; Top_Profile_Ref=582 mm; W=929 mm; W_Ref=904 mm
- 879-0500-00-044005599A0_DN500_PN10: Body_Collar_Dia=96 mm; Body_Collar_Dia_2=63 mm; Body_Flange_Dia=357 mm; Body_Flange_Dia_2=379 mm; Body_Height_1=357 mm; Body_Height_2=156 mm; Body_Height_3=330 mm; Body_Height_4=171 mm; Body_Top_Dia=42 mm  [stored 0.137795 ft]; Body_Top_Dia_2=35 mm  [stored 0.114829 ft]; Body_With_Dia=250 mm; Body_With_Dia_1=313 mm; Body_With_Dia_2=313 mm; Bolt_support=962 mm; Bolt_support_2=481 mm; Bolt_support_Dia=50 mm; Bolt_support_lenght=270 mm; Bolt_support_lenght_2=280 mm; Bottom_profile=125 mm; D1=291 mm; D3=335 mm; DN=500 mm; Fillet_Length=25 mm  [stored 0.082021 ft]; Fillet_Length_2=100 mm; Flange_thickness=32 mm  [stored 0.104987 ft]; H3=1408 mm; H3_Ref=1311 mm; H3_Ref_2=548 mm; ID=250 mm; L=1250 mm; PG_Dia=167 mm; PG_Ref=238 mm; PG_depth=35 mm  [stored 0.114829 ft]; PG_height=816 mm; PG_height_1=732 mm; PG_ref=260 mm; PR_1=124 mm; P_lenght=183 mm; Pilot_Dia_1=83 mm; Pilot_Dia_2=166 mm; Pilot_Dia_3=55 mm; Pilot_Dia_4=28 mm  [stored 0.0918635 ft]; Pilot_Dia_5=18 mm; Pilot_top_1=966 mm; Pilot_top_ref=97 mm; Profile1_Height=465 mm; Profile1_Length=91 mm; Profile1_Length_2=60 mm; Profile_Dia=25 mm  [stored 0.082021 ft]; Profile_Dia_2=25 mm  [stored 0.082021 ft]; Profile_Dia_3=50 mm; Profile_height ref=60 mm; T_Height=548 mm; T_Height_2=470 mm; T_Height_Ref_1=78 mm; T_Height_Ref_2=91 mm; Top_Profile=577 mm; Top_Profile_Ref=582 mm; W=929 mm; W_Ref=904 mm
- 879-0500-00-14400559999_DN500_PN16: Body_Collar_Dia=96 mm; Body_Collar_Dia_2=63 mm; Body_Flange_Dia=357 mm; Body_Flange_Dia_2=379 mm; Body_Height_1=357 mm; Body_Height_2=156 mm; Body_Height_3=180 mm; Body_Height_4=171 mm; Body_Top_Dia=42 mm  [stored 0.137795 ft]; Body_Top_Dia_2=35 mm  [stored 0.114829 ft]; Body_With_Dia=250 mm; Body_With_Dia_1=313 mm; Body_With_Dia_2=313 mm; Bolt_support=962 mm; Bolt_support_2=481 mm; Bolt_support_Dia=50 mm; Bolt_support_lenght=270 mm; Bolt_support_lenght_2=280 mm; Bottom_profile=125 mm; D1=305 mm; D3=358 mm; DN=500 mm; Fillet_Length=25 mm  [stored 0.082021 ft]; Fillet_Length_2=100 mm; Flange_thickness=32 mm  [stored 0.104987 ft]; H3=1245 mm; H3_Ref=1165 mm; H3_Ref_2=548 mm; ID=250 mm; L=1250 mm; PG_Dia=167 mm; PG_Ref=238 mm; PG_depth=35 mm  [stored 0.114829 ft]; PG_height=766 mm; PG_height_1=683 mm; PG_ref=260 mm; PR_1=84 mm; P_lenght=196 mm; Pilot_Dia_1=89 mm; Pilot_Dia_2=178 mm; Pilot_Dia_3=59 mm; Pilot_Dia_4=30 mm  [stored 0.0984252 ft]; Pilot_Dia_5=20 mm  [stored 0.0656168 ft]; Pilot_top_1=798 mm; Pilot_top_ref=80 mm; Profile1_Height=455 mm; Profile1_Length=97 mm; Profile1_Length_2=64 mm; Profile_Dia=25 mm  [stored 0.082021 ft]; Profile_Dia_2=25 mm  [stored 0.082021 ft]; Profile_Dia_3=50 mm; Profile_height ref=60 mm; T_Height=373 mm; T_Height_2=319 mm; T_Height_Ref_1=53 mm; T_Height_Ref_2=62 mm; Top_Profile=577 mm; Top_Profile_Ref=582 mm; W=929 mm; W_Ref=904 mm
- 879-0500-00-144005599A0_DN500_PN16: Body_Collar_Dia=96 mm; Body_Collar_Dia_2=63 mm; Body_Flange_Dia=357 mm; Body_Flange_Dia_2=379 mm; Body_Height_1=357 mm; Body_Height_2=156 mm; Body_Height_3=310 mm; Body_Height_4=171 mm; Body_Top_Dia=42 mm  [stored 0.137795 ft]; Body_Top_Dia_2=35 mm  [stored 0.114829 ft]; Body_With_Dia=250 mm; Body_With_Dia_1=313 mm; Body_With_Dia_2=313 mm; Bolt_support=962 mm; Bolt_support_2=481 mm; Bolt_support_Dia=50 mm; Bolt_support_lenght=270 mm; Bolt_support_lenght_2=280 mm; Bottom_profile=125 mm; D1=305 mm; D3=358 mm; DN=500 mm; Fillet_Length=25 mm  [stored 0.082021 ft]; Fillet_Length_2=100 mm; Flange_thickness=32 mm  [stored 0.104987 ft]; H3=1408 mm; H3_Ref=1312 mm; H3_Ref_2=548 mm; ID=250 mm; L=1250 mm; PG_Dia=167 mm; PG_Ref=238 mm; PG_depth=35 mm  [stored 0.114829 ft]; PG_height=803 mm; PG_height_1=720 mm; PG_ref=260 mm; PR_1=121 mm; P_lenght=196 mm; Pilot_Dia_1=89 mm; Pilot_Dia_2=178 mm; Pilot_Dia_3=59 mm; Pilot_Dia_4=30 mm  [stored 0.0984252 ft]; Pilot_Dia_5=20 mm  [stored 0.0656168 ft]; Pilot_top_1=944 mm; Pilot_top_ref=96 mm; Profile1_Height=455 mm; Profile1_Length=97 mm; Profile1_Length_2=64 mm; Profile_Dia=25 mm  [stored 0.082021 ft]; Profile_Dia_2=25 mm  [stored 0.082021 ft]; Profile_Dia_3=50 mm; Profile_height ref=60 mm; T_Height=536 mm; T_Height_2=459 mm; T_Height_Ref_1=77 mm; T_Height_Ref_2=89 mm; Top_Profile=577 mm; Top_Profile_Ref=582 mm; W=929 mm; W_Ref=904 mm
- 879-0600-00-04400559999_DN600_PN10: Body_Collar_Dia=112 mm; Body_Collar_Dia_2=73 mm; Body_Flange_Dia=414 mm; Body_Flange_Dia_2=439 mm; Body_Height_1=414 mm; Body_Height_2=181 mm; Body_Height_3=160 mm; Body_Height_4=196 mm; Body_Top_Dia=48 mm; Body_Top_Dia_2=40 mm  [stored 0.131234 ft]; Body_With_Dia=290 mm; Body_With_Dia_1=363 mm; Body_With_Dia_2=363 mm; Bolt_support=1115 mm; Bolt_support_2=558 mm; Bolt_support_Dia=60 mm; Bolt_support_lenght=320 mm; Bolt_support_lenght_2=330 mm; Bottom_profile=150 mm; D1=341 mm; D3=390 mm; DN=600 mm; Fillet_Length=30 mm  [stored 0.0984252 ft]; Fillet_Length_2=120 mm; Flange_thickness=36 mm  [stored 0.11811 ft]; H3=1355 mm; H3_Ref=1268 mm; H3_Ref_2=631 mm; ID=300 mm; L=1450 mm; PG_Dia=200 mm; PG_Ref=276 mm; PG_depth=42 mm  [stored 0.137795 ft]; PG_height=875 mm; PG_height_1=775 mm; PG_ref=310 mm; PR_1=85 mm; P_lenght=216 mm; Pilot_Dia_1=98 mm; Pilot_Dia_2=196 mm; Pilot_Dia_3=65 mm; Pilot_Dia_4=33 mm; Pilot_Dia_5=22 mm  [stored 0.0721785 ft]; Pilot_top_1=868 mm; Pilot_top_ref=87 mm; Profile1_Height=525 mm; Profile1_Length=105 mm; Profile1_Length_2=70 mm; Profile_Dia=30 mm  [stored 0.0984252 ft]; Profile_Dia_2=30 mm  [stored 0.0984252 ft]; Profile_Dia_3=60 mm; Profile_height ref=65 mm; T_Height=375 mm; T_Height_2=321 mm; T_Height_Ref_1=54 mm; T_Height_Ref_2=63 mm; Top_Profile=669 mm; Top_Profile_Ref=674 mm; W=1020 mm; W_Ref=990 mm
- 879-0600-00-044005599A0_DN600_PN10: Body_Collar_Dia=112 mm; Body_Collar_Dia_2=73 mm; Body_Flange_Dia=414 mm; Body_Flange_Dia_2=439 mm; Body_Height_1=414 mm; Body_Height_2=181 mm; Body_Height_3=300 mm; Body_Height_4=196 mm; Body_Top_Dia=48 mm; Body_Top_Dia_2=40 mm  [stored 0.131234 ft]; Body_With_Dia=290 mm; Body_With_Dia_1=363 mm; Body_With_Dia_2=363 mm; Bolt_support=1115 mm; Bolt_support_2=558 mm; Bolt_support_Dia=60 mm; Bolt_support_lenght=320 mm; Bolt_support_lenght_2=330 mm; Bottom_profile=150 mm; D1=341 mm; D3=390 mm; DN=600 mm; Fillet_Length=30 mm  [stored 0.0984252 ft]; Fillet_Length_2=120 mm; Flange_thickness=36 mm  [stored 0.11811 ft]; H3=1518 mm; H3_Ref=1419 mm; H3_Ref_2=631 mm; ID=300 mm; L=1450 mm; PG_Dia=200 mm; PG_Ref=276 mm; PG_depth=42 mm  [stored 0.137795 ft]; PG_height=919 mm; PG_height_1=819 mm; PG_ref=310 mm; PR_1=119 mm; P_lenght=216 mm; Pilot_Dia_1=98 mm; Pilot_Dia_2=196 mm; Pilot_Dia_3=65 mm; Pilot_Dia_4=33 mm; Pilot_Dia_5=22 mm  [stored 0.0721785 ft]; Pilot_top_1=1019 mm; Pilot_top_ref=99 mm; Profile1_Height=535 mm; Profile1_Length=105 mm; Profile1_Length_2=70 mm; Profile_Dia=30 mm  [stored 0.0984252 ft]; Profile_Dia_2=30 mm  [stored 0.0984252 ft]; Profile_Dia_3=60 mm; Profile_height ref=65 mm; T_Height=528 mm; T_Height_2=453 mm; T_Height_Ref_1=75 mm; T_Height_Ref_2=88 mm; Top_Profile=669 mm; Top_Profile_Ref=674 mm; W=1020 mm; W_Ref=990 mm
- 879-0600-00-14400559999_DN600_PN16: Body_Collar_Dia=112 mm; Body_Collar_Dia_2=73 mm; Body_Flange_Dia=414 mm; Body_Flange_Dia_2=439 mm; Body_Height_1=414 mm; Body_Height_2=181 mm; Body_Height_3=145 mm; Body_Height_4=196 mm; Body_Top_Dia=48 mm; Body_Top_Dia_2=40 mm  [stored 0.131234 ft]; Body_With_Dia=290 mm; Body_With_Dia_1=363 mm; Body_With_Dia_2=363 mm; Bolt_support=1115 mm; Bolt_support_2=558 mm; Bolt_support_Dia=60 mm; Bolt_support_lenght=320 mm; Bolt_support_lenght_2=330 mm; Bottom_profile=150 mm; D1=360 mm; D3=420 mm; DN=600 mm; Fillet_Length=30 mm  [stored 0.0984252 ft]; Fillet_Length_2=120 mm; Flange_thickness=36 mm  [stored 0.11811 ft]; H3=1355 mm; H3_Ref=1275 mm; H3_Ref_2=631 mm; ID=300 mm; L=1450 mm; PG_Dia=200 mm; PG_Ref=276 mm; PG_depth=42 mm  [stored 0.137795 ft]; PG_height=872 mm; PG_height_1=772 mm; PG_ref=310 mm; PR_1=77 mm; P_lenght=233 mm; Pilot_Dia_1=106 mm; Pilot_Dia_2=212 mm; Pilot_Dia_3=71 mm; Pilot_Dia_4=35 mm  [stored 0.114829 ft]; Pilot_Dia_5=24 mm  [stored 0.0787402 ft]; Pilot_top_1=845 mm; Pilot_top_ref=80 mm; Profile1_Height=530 mm; Profile1_Length=114 mm; Profile1_Length_2=76 mm; Profile_Dia=30 mm  [stored 0.0984252 ft]; Profile_Dia_2=30 mm  [stored 0.0984252 ft]; Profile_Dia_3=60 mm; Profile_height ref=65 mm; T_Height=340 mm; T_Height_2=291 mm; T_Height_Ref_1=49 mm; T_Height_Ref_2=57 mm; Top_Profile=669 mm; Top_Profile_Ref=674 mm; W=1020 mm; W_Ref=990 mm
- 879-0600-00-144005599A0_DN600_PN16: Body_Collar_Dia=112 mm; Body_Collar_Dia_2=73 mm; Body_Flange_Dia=414 mm; Body_Flange_Dia_2=439 mm; Body_Height_1=414 mm; Body_Height_2=181 mm; Body_Height_3=280 mm; Body_Height_4=196 mm; Body_Top_Dia=48 mm; Body_Top_Dia_2=40 mm  [stored 0.131234 ft]; Body_With_Dia=290 mm; Body_With_Dia_1=363 mm; Body_With_Dia_2=363 mm; Bolt_support=1115 mm; Bolt_support_2=558 mm; Bolt_support_Dia=60 mm; Bolt_support_lenght=320 mm; Bolt_support_lenght_2=330 mm; Bottom_profile=150 mm; D1=360 mm; D3=420 mm; DN=600 mm; Fillet_Length=30 mm  [stored 0.0984252 ft]; Fillet_Length_2=120 mm; Flange_thickness=36 mm  [stored 0.11811 ft]; H3=1518 mm; H3_Ref=1424 mm; H3_Ref_2=631 mm; ID=300 mm; L=1450 mm; PG_Dia=200 mm; PG_Ref=276 mm; PG_depth=42 mm  [stored 0.137795 ft]; PG_height=913 mm; PG_height_1=813 mm; PG_ref=310 mm; PR_1=113 mm; P_lenght=233 mm; Pilot_Dia_1=106 mm; Pilot_Dia_2=212 mm; Pilot_Dia_3=71 mm; Pilot_Dia_4=35 mm  [stored 0.114829 ft]; Pilot_Dia_5=24 mm  [stored 0.0787402 ft]; Pilot_top_1=994 mm; Pilot_top_ref=94 mm; Profile1_Height=535 mm; Profile1_Length=114 mm; Profile1_Length_2=76 mm; Profile_Dia=30 mm  [stored 0.0984252 ft]; Profile_Dia_2=30 mm  [stored 0.0984252 ft]; Profile_Dia_3=60 mm; Profile_height ref=65 mm; T_Height=498 mm; T_Height_2=427 mm; T_Height_Ref_1=71 mm; T_Height_Ref_2=83 mm; Top_Profile=669 mm; Top_Profile_Ref=674 mm; W=1020 mm; W_Ref=990 mm

note: [stored X ft] marks values corroborated as IEEE doubles in the binary element streams (Revit-internal decimal feet)

## geometry (parser evidence)
native form markers: Sweep x3
no freeform markers — native parametric forms only
